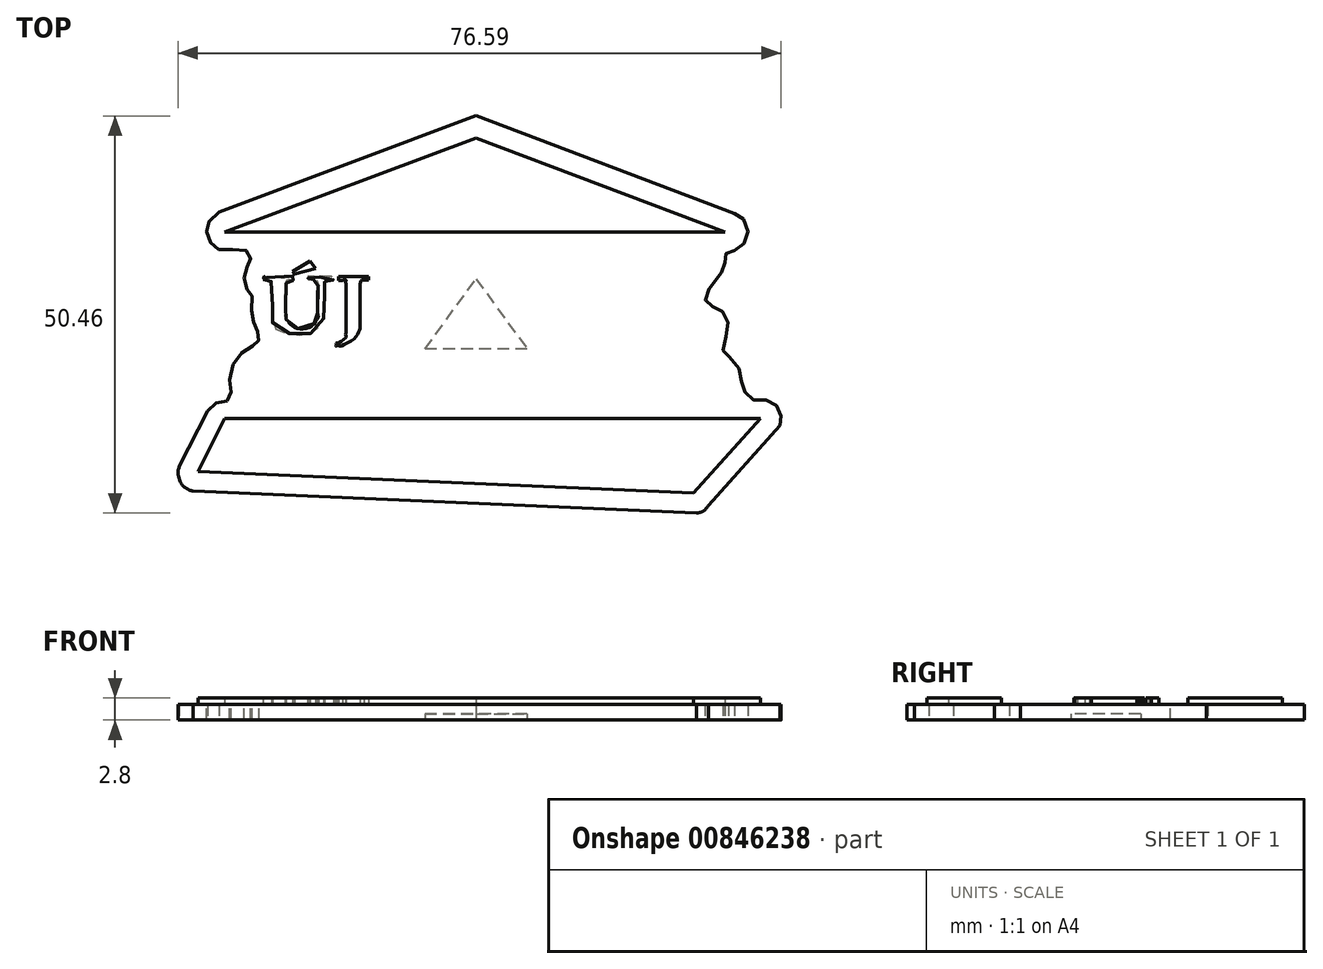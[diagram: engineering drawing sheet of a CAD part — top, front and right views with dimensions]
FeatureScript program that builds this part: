
annotation { "Feature Type Name" : "Feature", "Feature Type Description" : "" }
export const myFeature = defineFeature(function(context is Context, id is Id, definition is map)
    precondition{}
    {
        {
            var Q0;
            Q0=qCreatedBy(makeId("Top.planeOp"),FACE);
            var sketch = newSketch(context, id + "F0", { "sketchPlane" : qUnion([Q0])});
            skLineSegment(sketch, "E0", {"start": v(-30.08, 10.5) * mm, "end": v(1.83, 22.46) * mm});
            skLineSegment(sketch, "E1", {"start": v(1.83, 22.46) * mm, "end": v(33.46, 10.5) * mm});
            skLineSegment(sketch, "E2", {"start": v(33.46, 10.5) * mm, "end": v(-30.08, 10.5) * mm});
            skLineSegment(sketch, "E3", {"start": v(-30.08, -13.2) * mm, "end": v(37.96, -13.19) * mm});
            skLineSegment(sketch, "E4", {"start": v(37.96, -13.19) * mm, "end": v(29.5, -22.68) * mm});
            skLineSegment(sketch, "E5", {"start": v(29.5, -22.68) * mm, "end": v(-33.48, -19.9) * mm});
            skLineSegment(sketch, "E6", {"start": v(-33.48, -19.9) * mm, "end": v(-30.08, -13.2) * mm});
            skFitSpline(sketch, "E7", {"points": [v(-25.1, 4.44) * mm, v(-24.51, 4.46) * mm, v(-24.23, 4.28) * mm, v(-24.13, 3.89) * mm, v(-24.05, 0) * mm, v(-24.04, -0.4) * mm, v(-23.47, -1.49) * mm, v(-21.36, -2.34) * mm, v(-19.33, -2.17) * mm, v(-17.82, -0.87) * mm, v(-17.52, 0.4) * mm, v(-17.44, 3.46) * mm, v(-17.44, 3.92) * mm, v(-17.28, 4.2) * mm, v(-16.7, 4.4) * mm, v(-16.38, 4.41) * mm, v(-16.38, 4.8) * mm, v(-16.52, 4.86) * mm, v(-19.36, 4.89) * mm, v(-19.5, 4.87) * mm, v(-19.5, 4.8) * mm, v(-19.5, 4.47) * mm, v(-19.49, 4.38) * mm, v(-19.23, 4.43) * mm, v(-18.68, 4.41) * mm, v(-18.33, 4.24) * mm, v(-18.19, 3.78) * mm, v(-18.19, 3.5) * mm, v(-18.2, 0.13) * mm, v(-18.2, -0.14) * mm, v(-18.42, -0.62) * mm, v(-19.42, -1.46) * mm, v(-20.82, -1.61) * mm, v(-21.7, -1.14) * mm, v(-22.28, -0.2) * mm, v(-22.3, 0.46) * mm, v(-22.3, 0.68) * mm, v(-22.28, 3.9) * mm, v(-22.25, 4.08) * mm, v(-22.12, 4.32) * mm, v(-21.64, 4.43) * mm, v(-21.37, 4.43) * mm, v(-21.31, 4.6) * mm, v(-21.34, 4.74) * mm, v(-21.34, 4.89) * mm, v(-21.52, 4.89) * mm, v(-24.93, 4.84) * mm, v(-25.08, 4.86) * mm, v(-25.13, 4.71) * mm, v(-25.1, 4.44) * mm]});
            skLineSegment(sketch, "E8", {"start": v(-21.44, 5.5) * mm, "end": v(-21.2, 5.16) * mm});
            skLineSegment(sketch, "E9", {"start": v(-21.2, 5.16) * mm, "end": v(-18.55, 5.87) * mm});
            skLineSegment(sketch, "E10", {"start": v(-18.55, 5.87) * mm, "end": v(-19.2, 6.79) * mm});
            skLineSegment(sketch, "E11", {"start": v(-19.2, 6.79) * mm, "end": v(-21.44, 5.5) * mm});
            skLineSegment(sketch, "E12", {"start": v(-15.1, 4.36) * mm, "end": v(-15.63, 4.36) * mm});
            skLineSegment(sketch, "E13", {"start": v(-15.63, 4.36) * mm, "end": v(-15.63, 4.86) * mm});
            skLineSegment(sketch, "E14", {"start": v(-15.63, 4.86) * mm, "end": v(-11.81, 4.86) * mm});
            skLineSegment(sketch, "E15", {"start": v(-11.81, 4.86) * mm, "end": v(-11.81, 4.4) * mm});
            skLineSegment(sketch, "E16", {"start": v(-11.81, 4.4) * mm, "end": v(-12.34, 4.4) * mm});
            skLineSegment(sketch, "E17", {"start": v(-14.68, 4.01) * mm, "end": v(-14.68, -2.04) * mm});
            skLineSegment(sketch, "E18", {"start": v(-12.84, 4) * mm, "end": v(-12.84, -1.76) * mm});
            skFitSpline(sketch, "E19", {"points": [v(-15.1, 4.36) * mm, v(-14.78, 4.36) * mm, v(-14.68, 4.01) * mm], "startDerivative": vector(0.76, 0.17) * mm, "endDerivative": vector(0.08, -0.96) * mm});
            skFitSpline(sketch, "E20", {"points": [v(-12.84, 4) * mm, v(-12.68, 4.32) * mm, v(-12.34, 4.4) * mm], "startDerivative": vector(0.22, 0.75) * mm, "endDerivative": vector(0.8, 0.04) * mm});
            skFitSpline(sketch, "E21", {"points": [v(-14.68, -2.04) * mm, v(-14.68, -2.66) * mm, v(-14.68, -2.79) * mm, v(-15.17, -3.3) * mm, v(-15.78, -3.58) * mm, v(-15.9, -3.58) * mm, v(-15.89, -3.66) * mm, v(-15.9, -3.93) * mm, v(-15.78, -3.95) * mm, v(-15.43, -3.95) * mm, v(-14.92, -3.79) * mm, v(-13.75, -3.09) * mm, v(-13.2, -2.47) * mm, v(-12.84, -1.76) * mm], "startDerivative": vector(-0.26, -8.21) * mm, "endDerivative": vector(3.35, 7.13) * mm});
            skLineSegment(sketch, "E22", {"start": v(-8.39, 6.17) * mm, "end": v(-8.85, 6.17) * mm});
            skLineSegment(sketch, "E23", {"start": v(-8.85, 6.17) * mm, "end": v(-8.85, 6.78) * mm});
            skLineSegment(sketch, "E24", {"start": v(-8.85, 6.78) * mm, "end": v(-2.66, 6.78) * mm});
            skLineSegment(sketch, "E25", {"start": v(-2.66, 6.78) * mm, "end": v(-2.66, 6.17) * mm});
            skLineSegment(sketch, "E26", {"start": v(-2.66, 6.17) * mm, "end": v(-3.36, 6.17) * mm});
            skLineSegment(sketch, "E27", {"start": v(-7.13, 5.37) * mm, "end": v(-7.13, -2.82) * mm});
            skLineSegment(sketch, "E28", {"start": v(-4.27, 5.39) * mm, "end": v(-4.27, 2.06) * mm});
            skLineSegment(sketch, "E29", {"start": v(-4.27, 2.06) * mm, "end": v(0.72, 2.06) * mm});
            skLineSegment(sketch, "E30", {"start": v(0.72, 2.06) * mm, "end": v(0.72, 5.28) * mm});
            skLineSegment(sketch, "E31", {"start": v(-0.41, 6.13) * mm, "end": v(-0.88, 6.13) * mm});
            skLineSegment(sketch, "E32", {"start": v(-0.88, 6.13) * mm, "end": v(-0.88, 6.7) * mm});
            skLineSegment(sketch, "E33", {"start": v(-0.88, 6.7) * mm, "end": v(5.27, 6.7) * mm});
            skLineSegment(sketch, "E34", {"start": v(5.27, 6.7) * mm, "end": v(5.27, 6.19) * mm});
            skLineSegment(sketch, "E35", {"start": v(5.27, 6.19) * mm, "end": v(4.53, 6.19) * mm});
            skLineSegment(sketch, "E36", {"start": v(3.5, 5.2) * mm, "end": v(3.5, -2.7) * mm});
            skLineSegment(sketch, "E37", {"start": v(-4.28, -2.78) * mm, "end": v(-4.28, 1.1) * mm});
            skLineSegment(sketch, "E38", {"start": v(-4.28, 1.1) * mm, "end": v(0.7, 1.1) * mm});
            skLineSegment(sketch, "E39", {"start": v(0.7, 1.1) * mm, "end": v(0.7, -2.6) * mm});
            skLineSegment(sketch, "E40", {"start": v(-8.5, -3.66) * mm, "end": v(-8.85, -3.66) * mm});
            skLineSegment(sketch, "E41", {"start": v(-8.85, -3.66) * mm, "end": v(-8.85, -4.23) * mm});
            skLineSegment(sketch, "E42", {"start": v(-8.85, -4.23) * mm, "end": v(-2.68, -4.23) * mm});
            skLineSegment(sketch, "E43", {"start": v(-2.68, -4.23) * mm, "end": v(-2.68, -3.75) * mm});
            skLineSegment(sketch, "E44", {"start": v(-2.68, -3.75) * mm, "end": v(-3.08, -3.75) * mm});
            skLineSegment(sketch, "E45", {"start": v(-0.67, -3.75) * mm, "end": v(-1, -3.75) * mm});
            skLineSegment(sketch, "E46", {"start": v(-1, -3.75) * mm, "end": v(-1, -4.23) * mm});
            skLineSegment(sketch, "E47", {"start": v(-1, -4.23) * mm, "end": v(5.21, -4.23) * mm});
            skLineSegment(sketch, "E48", {"start": v(5.21, -4.23) * mm, "end": v(5.21, -3.75) * mm});
            skLineSegment(sketch, "E49", {"start": v(5.21, -3.75) * mm, "end": v(4.72, -3.75) * mm});
            skLineSegment(sketch, "E50", {"start": v(6.1, -3.75) * mm, "end": v(5.78, -3.75) * mm});
            skLineSegment(sketch, "E51", {"start": v(5.78, -3.75) * mm, "end": v(5.78, -4.23) * mm});
            skLineSegment(sketch, "E52", {"start": v(5.78, -4.23) * mm, "end": v(10.42, -4.23) * mm});
            skLineSegment(sketch, "E53", {"start": v(10.42, -4.23) * mm, "end": v(10.42, -3.75) * mm});
            skLineSegment(sketch, "E54", {"start": v(10.42, -3.75) * mm, "end": v(10.07, -3.75) * mm});
            skLineSegment(sketch, "E55", {"start": v(7.73, -2.6) * mm, "end": v(12.18, 6.83) * mm});
            skLineSegment(sketch, "E56", {"start": v(12.18, 6.83) * mm, "end": v(13.26, 6.83) * mm});
            skLineSegment(sketch, "E57", {"start": v(13.26, 6.83) * mm, "end": v(17.45, -2.7) * mm});
            skLineSegment(sketch, "E58", {"start": v(10.22, 0) * mm, "end": v(11.72, 3.76) * mm});
            skLineSegment(sketch, "E59", {"start": v(11.72, 3.76) * mm, "end": v(13.22, 0) * mm});
            skLineSegment(sketch, "E60", {"start": v(13.22, 0) * mm, "end": v(10.22, 0) * mm});
            skLineSegment(sketch, "E61", {"start": v(8.99, -3) * mm, "end": v(9.81, -0.88) * mm});
            skLineSegment(sketch, "E62", {"start": v(9.81, -0.88) * mm, "end": v(13.66, -0.88) * mm});
            skLineSegment(sketch, "E63", {"start": v(13.66, -0.88) * mm, "end": v(14.56, -3.07) * mm});
            skLineSegment(sketch, "E64", {"start": v(13.8, -3.75) * mm, "end": v(13.43, -3.75) * mm});
            skLineSegment(sketch, "E65", {"start": v(13.43, -3.75) * mm, "end": v(13.43, -4.23) * mm});
            skLineSegment(sketch, "E66", {"start": v(13.43, -4.23) * mm, "end": v(19.3, -4.23) * mm});
            skLineSegment(sketch, "E67", {"start": v(19.3, -4.23) * mm, "end": v(19.3, -3.75) * mm});
            skLineSegment(sketch, "E68", {"start": v(19.3, -3.75) * mm, "end": v(18.88, -3.75) * mm});
            skLineSegment(sketch, "E69", {"start": v(11.34, 7.83) * mm, "end": v(11.73, 7.26) * mm});
            skLineSegment(sketch, "E70", {"start": v(11.73, 7.26) * mm, "end": v(16.2, 8.38) * mm});
            skLineSegment(sketch, "E71", {"start": v(16.2, 8.38) * mm, "end": v(15.06, 9.86) * mm});
            skLineSegment(sketch, "E72", {"start": v(15.06, 9.86) * mm, "end": v(11.34, 7.83) * mm});
            skLineSegment(sketch, "E73", {"start": v(23.23, 6.07) * mm, "end": v(27.17, 6.07) * mm});
            skLineSegment(sketch, "E74", {"start": v(27.17, 6.07) * mm, "end": v(19.8, -3.96) * mm});
            skLineSegment(sketch, "E75", {"start": v(19.8, -3.96) * mm, "end": v(20, -4.32) * mm});
            skLineSegment(sketch, "E76", {"start": v(20, -4.32) * mm, "end": v(30.47, -4.32) * mm});
            skLineSegment(sketch, "E77", {"start": v(30.47, -4.32) * mm, "end": v(31.28, -1.27) * mm});
            skLineSegment(sketch, "E78", {"start": v(31.28, -1.27) * mm, "end": v(30.49, -1.27) * mm});
            skLineSegment(sketch, "E79", {"start": v(30.49, -1.27) * mm, "end": v(29.93, -2.28) * mm});
            skLineSegment(sketch, "E80", {"start": v(27.89, -3.5) * mm, "end": v(23.51, -3.5) * mm});
            skLineSegment(sketch, "E81", {"start": v(23.51, -3.5) * mm, "end": v(30.8, 6.4) * mm});
            skLineSegment(sketch, "E82", {"start": v(30.8, 6.4) * mm, "end": v(30.6, 6.77) * mm});
            skLineSegment(sketch, "E83", {"start": v(30.6, 6.77) * mm, "end": v(22.29, 6.77) * mm});
            skLineSegment(sketch, "E84", {"start": v(21.5, 7.2) * mm, "end": v(20.84, 7.2) * mm});
            skLineSegment(sketch, "E85", {"start": v(20.84, 7.2) * mm, "end": v(20.84, 3.95) * mm});
            skLineSegment(sketch, "E86", {"start": v(20.84, 3.95) * mm, "end": v(21.5, 3.95) * mm});
            skFitSpline(sketch, "E87", {"points": [v(-8.39, 6.17) * mm, v(-7.89, 6.17) * mm, v(-7.38, 5.86) * mm, v(-7.13, 5.37) * mm], "startDerivative": vector(1.55, 0.19) * mm, "endDerivative": vector(0.57, -1.56) * mm});
            skFitSpline(sketch, "E88", {"points": [v(-4.27, 5.39) * mm, v(-4.1, 5.83) * mm, v(-3.74, 6.05) * mm, v(-3.36, 6.17) * mm], "startDerivative": vector(0.33, 1.4) * mm, "endDerivative": vector(1.17, 0.33) * mm});
            skFitSpline(sketch, "E89", {"points": [v(-7.13, -2.82) * mm, v(-7.28, -3.3) * mm, v(-7.7, -3.6) * mm, v(-8.23, -3.66) * mm, v(-8.5, -3.66) * mm], "startDerivative": vector(-0.35, -1.9) * mm, "endDerivative": vector(-1.25, 0.02) * mm});
            skFitSpline(sketch, "E90", {"points": [v(-4.28, -2.78) * mm, v(-4.1, -3.18) * mm, v(-3.76, -3.5) * mm, v(-3.08, -3.75) * mm], "startDerivative": vector(0.48, -1.4) * mm, "endDerivative": vector(1.91, -0.58) * mm});
            skFitSpline(sketch, "E91", {"points": [v(-0.67, -3.75) * mm, v(-0.24, -3.75) * mm, v(0.3, -3.66) * mm, v(0.65, -3.2) * mm, v(0.7, -2.6) * mm], "startDerivative": vector(1.82, 0) * mm, "endDerivative": vector(-0.04, 2.27) * mm});
            skFitSpline(sketch, "E92", {"points": [v(3.5, -2.7) * mm, v(3.72, -3.17) * mm, v(4.05, -3.48) * mm, v(4.41, -3.66) * mm, v(4.72, -3.75) * mm], "startDerivative": vector(0.63, -1.81) * mm, "endDerivative": vector(1.39, -0.34) * mm});
            skFitSpline(sketch, "E93", {"points": [v(6.1, -3.75) * mm, v(6.63, -3.75) * mm, v(7.2, -3.43) * mm, v(7.73, -2.6) * mm], "startDerivative": vector(1.82, -0.19) * mm, "endDerivative": vector(1.2, 2.39) * mm});
            skFitSpline(sketch, "E94", {"points": [v(8.99, -3) * mm, v(8.99, -3.18) * mm, v(9.13, -3.44) * mm, v(9.5, -3.63) * mm, v(10.07, -3.75) * mm], "startDerivative": vector(-0.22, -1.52) * mm, "endDerivative": vector(2.37, -0.06) * mm});
            skFitSpline(sketch, "E95", {"points": [v(-0.41, 6.13) * mm, v(0, 6.13) * mm, v(0.32, 5.98) * mm, v(0.54, 5.77) * mm, v(0.67, 5.45) * mm, v(0.72, 5.28) * mm], "startDerivative": vector(1.85, 0.19) * mm, "endDerivative": vector(0.28, -1) * mm});
            skFitSpline(sketch, "E96", {"points": [v(3.5, 5.2) * mm, v(3.5, 5.55) * mm, v(3.71, 5.87) * mm, v(4.07, 6.13) * mm, v(4.53, 6.19) * mm], "startDerivative": vector(-0.19, 1.53) * mm, "endDerivative": vector(1.8, 0.02) * mm});
            skFitSpline(sketch, "E97", {"points": [v(13.8, -3.75) * mm, v(14.03, -3.75) * mm, v(14.36, -3.59) * mm, v(14.5, -3.41) * mm, v(14.56, -3.07) * mm], "startDerivative": vector(0.97, -0.13) * mm, "endDerivative": vector(0.08, 1.38) * mm});
            skFitSpline(sketch, "E98", {"points": [v(17.45, -2.7) * mm, v(17.64, -2.98) * mm, v(17.94, -3.34) * mm, v(18.22, -3.52) * mm, v(18.6, -3.68) * mm, v(18.88, -3.75) * mm], "startDerivative": vector(0.89, -1.38) * mm, "endDerivative": vector(1.49, -0.33) * mm});
            skFitSpline(sketch, "E99", {"points": [v(21.5, 7.2) * mm, v(21.67, 6.98) * mm, v(21.93, 6.8) * mm, v(22.29, 6.77) * mm], "startDerivative": vector(0.55, -0.66) * mm, "endDerivative": vector(1.06, 0.06) * mm});
            skFitSpline(sketch, "E100", {"points": [v(21.5, 3.95) * mm, v(21.57, 4.4) * mm, v(21.78, 4.93) * mm, v(22.1, 5.4) * mm, v(22.64, 5.85) * mm, v(23.23, 6.07) * mm], "startDerivative": vector(0.3, 2.51) * mm, "endDerivative": vector(2.87, 0.8) * mm});
            skFitSpline(sketch, "E101", {"points": [v(27.89, -3.5) * mm, v(28.28, -3.5) * mm, v(28.84, -3.34) * mm, v(29.28, -3.05) * mm, v(29.7, -2.6) * mm, v(29.93, -2.28) * mm], "startDerivative": vector(2.09, -0.14) * mm, "endDerivative": vector(1.15, 1.72) * mm});
            skFitSpline(sketch, "E102", {"points": [v(-18.55, -5.16) * mm, v(-19.5, -5.13) * mm, v(-21.12, -5.07) * mm, v(-22, -5.07) * mm, v(-22.58, -5.12) * mm, v(-23.16, -5.22) * mm, v(-23.92, -5.38) * mm, v(-24.9, -5.72) * mm, v(-25.9, -6.27) * mm, v(-26.51, -6.9) * mm, v(-26.87, -7.57) * mm, v(-27, -8.39) * mm, v(-26.85, -9.23) * mm, v(-26.55, -9.8) * mm, v(-26.01, -10.28) * mm, v(-25.25, -10.75) * mm, v(-23.93, -11.23) * mm, v(-22.44, -11.46) * mm, v(-20.86, -11.5) * mm, v(-19.93, -11.43) * mm, v(-19.02, -11.34) * mm, v(-18.6, -11.26) * mm, v(-18.57, -11.26) * mm, v(-18.48, -11.07) * mm, v(-18.1, -10.43) * mm, v(-17.75, -9.8) * mm, v(-17.71, -9.74) * mm, v(-17.8, -9.71) * mm, v(-18.35, -9.68) * mm, v(-18.4, -9.67) * mm, v(-18.46, -9.74) * mm, v(-18.56, -9.88) * mm, v(-18.93, -10.27) * mm, v(-19.68, -10.75) * mm, v(-20.35, -10.95) * mm, v(-21.57, -11) * mm, v(-22.99, -10.7) * mm, v(-23.78, -10.03) * mm, v(-24.3, -9.17) * mm, v(-24.47, -7.92) * mm, v(-24.2, -6.98) * mm, v(-23.84, -6.46) * mm, v(-23.06, -5.94) * mm, v(-22.3, -5.64) * mm, v(-21.27, -5.47) * mm, v(-20.47, -5.49) * mm, v(-20, -5.61) * mm, v(-19.36, -5.96) * mm, v(-18.97, -6.34) * mm, v(-18.7, -6.63) * mm, v(-18.63, -6.81) * mm, v(-18.62, -6.84) * mm, v(-18.53, -6.87) * mm, v(-18.08, -6.84) * mm, v(-18.05, -6.82) * mm, v(-18.08, -6.52) * mm, v(-18.1, -6.12) * mm, v(-18.13, -5.6) * mm, v(-18.22, -5.17) * mm, v(-18.55, -5.16) * mm]});
            skLineSegment(sketch, "E103", {"start": v(-14.56, -8.57) * mm, "end": v(-12.39, -8.57) * mm});
            skLineSegment(sketch, "E104", {"start": v(-14.61, -9) * mm, "end": v(-10.44, -9) * mm});
            skLineSegment(sketch, "E105", {"start": v(-9.34, -11) * mm, "end": v(-9.63, -11) * mm});
            skLineSegment(sketch, "E106", {"start": v(-9.63, -11) * mm, "end": v(-9.63, -11.37) * mm});
            skLineSegment(sketch, "E107", {"start": v(-9.63, -11.37) * mm, "end": v(-5.63, -11.37) * mm});
            skLineSegment(sketch, "E108", {"start": v(-5.63, -11.37) * mm, "end": v(-5.63, -10.98) * mm});
            skLineSegment(sketch, "E109", {"start": v(-5.63, -10.98) * mm, "end": v(-5.8, -11) * mm});
            skLineSegment(sketch, "E110", {"start": v(-8.57, -7.94) * mm, "end": v(-8.57, -10.62) * mm});
            skLineSegment(sketch, "E111", {"start": v(-6.5, -7.96) * mm, "end": v(-6.5, -10.59) * mm});
            skLineSegment(sketch, "E112", {"start": v(-4.21, -8.3) * mm, "end": v(-4.21, -10.74) * mm});
            skLineSegment(sketch, "E113", {"start": v(-4.69, -10.98) * mm, "end": v(-4.98, -10.98) * mm});
            skLineSegment(sketch, "E114", {"start": v(-4.98, -10.98) * mm, "end": v(-4.98, -11.37) * mm});
            skLineSegment(sketch, "E115", {"start": v(-4.98, -11.37) * mm, "end": v(-1.1, -11.37) * mm});
            skLineSegment(sketch, "E116", {"start": v(-1.1, -11.37) * mm, "end": v(-1.1, -10.98) * mm});
            skLineSegment(sketch, "E117", {"start": v(-1.1, -10.98) * mm, "end": v(-1.33, -10.98) * mm});
            skLineSegment(sketch, "E118", {"start": v(-2.04, -8.28) * mm, "end": v(-2.04, -10.69) * mm});
            skLineSegment(sketch, "E119", {"start": v(2.64, -10.35) * mm, "end": v(2.64, -7.53) * mm});
            skLineSegment(sketch, "E120", {"start": v(2.64, -7.53) * mm, "end": v(4.31, -7.53) * mm});
            skLineSegment(sketch, "E121", {"start": v(4.31, -7.53) * mm, "end": v(4.31, -7.02) * mm});
            skLineSegment(sketch, "E122", {"start": v(4.31, -7.02) * mm, "end": v(2.64, -7.02) * mm});
            skLineSegment(sketch, "E123", {"start": v(2.64, -7.02) * mm, "end": v(2.64, -5.7) * mm});
            skLineSegment(sketch, "E124", {"start": v(2.64, -5.7) * mm, "end": v(2.15, -5.7) * mm});
            skLineSegment(sketch, "E125", {"start": v(2.15, -5.7) * mm, "end": v(0.43, -6.4) * mm});
            skLineSegment(sketch, "E126", {"start": v(0.43, -6.4) * mm, "end": v(0.43, -7.02) * mm});
            skLineSegment(sketch, "E127", {"start": v(0.43, -7.02) * mm, "end": v(-0.2, -7.02) * mm});
            skLineSegment(sketch, "E128", {"start": v(-0.2, -7.02) * mm, "end": v(-0.73, -7.53) * mm});
            skLineSegment(sketch, "E129", {"start": v(-0.73, -7.53) * mm, "end": v(0.43, -7.53) * mm});
            skLineSegment(sketch, "E130", {"start": v(0.43, -7.53) * mm, "end": v(0.43, -10.53) * mm});
            skLineSegment(sketch, "E131", {"start": v(6.13, -8.07) * mm, "end": v(6.13, -10.53) * mm});
            skLineSegment(sketch, "E132", {"start": v(8.26, -8.42) * mm, "end": v(8.26, -10.6) * mm});
            skLineSegment(sketch, "E133", {"start": v(5.37, -11) * mm, "end": v(5.06, -11) * mm});
            skLineSegment(sketch, "E134", {"start": v(5.06, -11) * mm, "end": v(5.06, -11.36) * mm});
            skLineSegment(sketch, "E135", {"start": v(5.06, -11.36) * mm, "end": v(9.5, -11.36) * mm});
            skLineSegment(sketch, "E136", {"start": v(9.5, -11.36) * mm, "end": v(9.5, -10.98) * mm});
            skLineSegment(sketch, "E137", {"start": v(9.5, -10.98) * mm, "end": v(8.93, -10.98) * mm});
            skLineSegment(sketch, "E138", {"start": v(8.26, -7.93) * mm, "end": v(8.26, -6.9) * mm});
            skLineSegment(sketch, "E139", {"start": v(5.53, -7.62) * mm, "end": v(5.24, -7.62) * mm});
            skLineSegment(sketch, "E140", {"start": v(5.24, -7.62) * mm, "end": v(5.24, -7.3) * mm});
            skLineSegment(sketch, "E141", {"start": v(5.24, -7.3) * mm, "end": v(6.13, -7.3) * mm});
            skLineSegment(sketch, "E142", {"start": v(14.85, -9.91) * mm, "end": v(14.85, -7.04) * mm});
            skLineSegment(sketch, "E143", {"start": v(14.85, -7.04) * mm, "end": v(11.89, -7.14) * mm});
            skLineSegment(sketch, "E144", {"start": v(11.89, -7.14) * mm, "end": v(11.9, -7.54) * mm});
            skLineSegment(sketch, "E145", {"start": v(12.77, -7.86) * mm, "end": v(12.77, -10.35) * mm});
            skLineSegment(sketch, "E146", {"start": v(19.3, -10.56) * mm, "end": v(19.3, -7.08) * mm});
            skLineSegment(sketch, "E147", {"start": v(19.3, -7.08) * mm, "end": v(16.1, -7.17) * mm});
            skLineSegment(sketch, "E148", {"start": v(16.1, -7.17) * mm, "end": v(16.11, -7.5) * mm});
            skLineSegment(sketch, "E149", {"start": v(17.07, -7.77) * mm, "end": v(17.07, -10.43) * mm});
            skLineSegment(sketch, "E150", {"start": v(17.06, -10.88) * mm, "end": v(17.06, -11.45) * mm});
            skLineSegment(sketch, "E151", {"start": v(21.75, -7.23) * mm, "end": v(21.11, -7.23) * mm});
            skLineSegment(sketch, "E152", {"start": v(21.11, -7.23) * mm, "end": v(21.12, -7.6) * mm});
            skLineSegment(sketch, "E153", {"start": v(21.12, -7.6) * mm, "end": v(21.56, -7.6) * mm});
            skLineSegment(sketch, "E154", {"start": v(21.94, -7.89) * mm, "end": v(21.94, -10.72) * mm});
            skLineSegment(sketch, "E155", {"start": v(24.11, -8.08) * mm, "end": v(24.11, -10.75) * mm});
            skLineSegment(sketch, "E156", {"start": v(26.3, -8.31) * mm, "end": v(26.3, -10.76) * mm});
            skLineSegment(sketch, "E157", {"start": v(28.55, -8.04) * mm, "end": v(28.55, -10.73) * mm});
            skLineSegment(sketch, "E158", {"start": v(30.73, -8.35) * mm, "end": v(30.73, -10.82) * mm});
            skLineSegment(sketch, "E159", {"start": v(32.95, -8.3) * mm, "end": v(32.95, -10.75) * mm});
            skLineSegment(sketch, "E160", {"start": v(21.07, -11.02) * mm, "end": v(20.93, -11.02) * mm});
            skLineSegment(sketch, "E161", {"start": v(20.93, -11.02) * mm, "end": v(20.93, -11.4) * mm});
            skLineSegment(sketch, "E162", {"start": v(20.93, -11.4) * mm, "end": v(24.9, -11.4) * mm});
            skLineSegment(sketch, "E163", {"start": v(24.9, -11.4) * mm, "end": v(24.88, -11) * mm});
            skLineSegment(sketch, "E164", {"start": v(24.88, -11) * mm, "end": v(24.61, -11.02) * mm});
            skLineSegment(sketch, "E165", {"start": v(25.73, -11) * mm, "end": v(25.55, -11) * mm});
            skLineSegment(sketch, "E166", {"start": v(25.55, -11) * mm, "end": v(25.55, -11.4) * mm});
            skLineSegment(sketch, "E167", {"start": v(25.55, -11.4) * mm, "end": v(29.38, -11.4) * mm});
            skLineSegment(sketch, "E168", {"start": v(29.38, -11.4) * mm, "end": v(29.36, -11) * mm});
            skLineSegment(sketch, "E169", {"start": v(29.36, -11) * mm, "end": v(29.06, -11.02) * mm});
            skLineSegment(sketch, "E170", {"start": v(30.22, -11) * mm, "end": v(29.94, -11) * mm});
            skLineSegment(sketch, "E171", {"start": v(29.94, -11) * mm, "end": v(29.94, -11.4) * mm});
            skLineSegment(sketch, "E172", {"start": v(29.94, -11.4) * mm, "end": v(33.83, -11.4) * mm});
            skLineSegment(sketch, "E173", {"start": v(33.83, -11.4) * mm, "end": v(33.83, -10.97) * mm});
            skLineSegment(sketch, "E174", {"start": v(33.83, -10.97) * mm, "end": v(33.61, -10.98) * mm});
            skLineSegment(sketch, "E175", {"start": v(24.15, -7.62) * mm, "end": v(24.15, -6.96) * mm});
            skFitSpline(sketch, "E176", {"points": [v(33.61, -10.98) * mm, v(33.42, -10.98) * mm, v(33.1, -10.86) * mm, v(32.95, -10.75) * mm], "startDerivative": vector(-0.59, -0.06) * mm, "endDerivative": vector(-0.4, 0.42) * mm});
            skFitSpline(sketch, "E177", {"points": [v(32.95, -8.3) * mm, v(32.85, -7.9) * mm, v(32.66, -7.6) * mm, v(32.23, -7.27) * mm, v(31.7, -7.1) * mm, v(31.1, -6.98) * mm, v(30.3, -7) * mm, v(29.68, -7.15) * mm, v(29.1, -7.4) * mm, v(28.67, -7.62) * mm, v(28.4, -7.78) * mm, v(28.36, -7.79) * mm, v(28.32, -7.7) * mm, v(27.99, -7.33) * mm, v(27.45, -7.06) * mm, v(26.78, -6.96) * mm, v(25.91, -7) * mm, v(25.4, -7.11) * mm, v(24.68, -7.38) * mm, v(24.41, -7.52) * mm, v(24.15, -7.62) * mm], "startDerivative": vector(-1.81, 8.83) * mm, "endDerivative": vector(-7.1, -2.45) * mm});
            skFitSpline(sketch, "E178", {"points": [v(30.22, -11) * mm, v(30.4, -11) * mm, v(30.6, -10.96) * mm, v(30.73, -10.82) * mm], "startDerivative": vector(0.55, -0.04) * mm, "endDerivative": vector(0.32, 0.72) * mm});
            skFitSpline(sketch, "E179", {"points": [v(28.55, -10.73) * mm, v(28.68, -10.9) * mm, v(28.84, -10.97) * mm, v(29.06, -11.02) * mm], "startDerivative": vector(0.37, -0.56) * mm, "endDerivative": vector(0.68, -0.1) * mm});
            skFitSpline(sketch, "E180", {"points": [v(28.55, -8.04) * mm, v(28.7, -7.94) * mm, v(29.24, -7.76) * mm, v(29.59, -7.73) * mm, v(29.95, -7.73) * mm, v(30.43, -7.87) * mm, v(30.68, -8.15) * mm, v(30.73, -8.35) * mm], "startDerivative": vector(1.2, 0.86) * mm, "endDerivative": vector(1.1, -1.57) * mm});
            skFitSpline(sketch, "E181", {"points": [v(26.3, -8.31) * mm, v(26.23, -8.14) * mm, v(26.06, -7.96) * mm, v(25.87, -7.82) * mm, v(25.27, -7.7) * mm, v(24.9, -7.7) * mm, v(24.36, -7.86) * mm, v(24.19, -7.96) * mm, v(24.11, -8.08) * mm], "startDerivative": vector(-0.53, 1.8) * mm, "endDerivative": vector(-0.74, -1.45) * mm});
            skFitSpline(sketch, "E182", {"points": [v(25.73, -11) * mm, v(25.87, -11) * mm, v(26.05, -10.96) * mm, v(26.23, -10.86) * mm, v(26.3, -10.76) * mm], "startDerivative": vector(0.62, -0.04) * mm, "endDerivative": vector(0.28, 0.48) * mm});
            skFitSpline(sketch, "E183", {"points": [v(24.11, -10.75) * mm, v(24.17, -10.86) * mm, v(24.29, -10.96) * mm, v(24.5, -11) * mm, v(24.61, -11.02) * mm], "startDerivative": vector(0.2, -0.51) * mm, "endDerivative": vector(0.46, -0.05) * mm});
            skFitSpline(sketch, "E184", {"points": [v(24.15, -6.96) * mm, v(23.92, -7.04) * mm, v(22.83, -7.2) * mm, v(21.75, -7.23) * mm], "startDerivative": vector(-0.95, -0.4) * mm, "endDerivative": vector(-2.53, -0.03) * mm});
            skFitSpline(sketch, "E185", {"points": [v(21.56, -7.6) * mm, v(21.67, -7.65) * mm, v(21.86, -7.77) * mm, v(21.94, -7.89) * mm], "startDerivative": vector(0.36, -0.15) * mm, "endDerivative": vector(0.2, -0.4) * mm});
            skFitSpline(sketch, "E186", {"points": [v(21.94, -10.72) * mm, v(21.87, -10.8) * mm, v(21.68, -10.93) * mm, v(21.26, -11.02) * mm, v(21.07, -11.02) * mm], "startDerivative": vector(-0.28, -0.62) * mm, "endDerivative": vector(-0.73, 0.03) * mm});
            skFitSpline(sketch, "E187", {"points": [v(17.06, -11.45) * mm, v(17.7, -11.33) * mm, v(18.22, -11.26) * mm, v(18.78, -11.19) * mm, v(19.6, -11.1) * mm, v(20.24, -11.1) * mm, v(20.27, -11.09) * mm, v(20.27, -10.9) * mm, v(20.24, -10.72) * mm, v(19.91, -10.72) * mm, v(19.3, -10.56) * mm], "startDerivative": vector(3.34, 1) * mm, "endDerivative": vector(-2.67, 2.3) * mm});
            skFitSpline(sketch, "E188", {"points": [v(16.11, -7.5) * mm, v(16.3, -7.5) * mm, v(16.55, -7.5) * mm, v(16.84, -7.6) * mm, v(17.07, -7.77) * mm], "startDerivative": vector(0.84, -0.02) * mm, "endDerivative": vector(0.84, -0.69) * mm});
            skFitSpline(sketch, "E189", {"points": [v(14.85, -9.91) * mm, v(14.93, -10.17) * mm, v(15.05, -10.4) * mm, v(15.4, -10.67) * mm, v(15.7, -10.74) * mm, v(16.11, -10.75) * mm, v(16.52, -10.7) * mm, v(16.8, -10.6) * mm, v(17.07, -10.43) * mm], "startDerivative": vector(0.65, -2.37) * mm, "endDerivative": vector(2.2, 1.56) * mm});
            skFitSpline(sketch, "E190", {"points": [v(12.77, -10.35) * mm, v(12.77, -10.5) * mm, v(12.83, -10.66) * mm, v(12.98, -10.88) * mm, v(13.37, -11.15) * mm, v(13.88, -11.38) * mm, v(14.52, -11.47) * mm, v(15.32, -11.48) * mm, v(15.85, -11.36) * mm, v(16.43, -11.15) * mm, v(16.76, -11) * mm, v(17.06, -10.88) * mm], "startDerivative": vector(-0.25, -2.77) * mm, "endDerivative": vector(3.84, 1.33) * mm});
            skFitSpline(sketch, "E191", {"points": [v(11.9, -7.54) * mm, v(12.1, -7.54) * mm, v(12.4, -7.6) * mm, v(12.64, -7.7) * mm, v(12.77, -7.86) * mm], "startDerivative": vector(0.84, 0.04) * mm, "endDerivative": vector(0.44, -0.83) * mm});
            skFitSpline(sketch, "E192", {"points": [v(6.13, -7.3) * mm, v(6.3, -7.3) * mm, v(6.7, -7.23) * mm, v(7.26, -7.12) * mm, v(7.83, -6.98) * mm, v(8.26, -6.9) * mm], "startDerivative": vector(1.3, -0.06) * mm, "endDerivative": vector(2.6, 0.65) * mm});
            skFitSpline(sketch, "E193", {"points": [v(5.53, -7.62) * mm, v(5.66, -7.65) * mm, v(5.94, -7.73) * mm, v(6.07, -7.87) * mm, v(6.13, -8.07) * mm], "startDerivative": vector(0.58, -0.13) * mm, "endDerivative": vector(0.16, -0.83) * mm});
            skFitSpline(sketch, "E194", {"points": [v(6.13, -10.53) * mm, v(6.08, -10.68) * mm, v(5.97, -10.83) * mm, v(5.74, -10.96) * mm, v(5.49, -11.01) * mm, v(5.37, -11) * mm], "startDerivative": vector(-0.24, -0.84) * mm, "endDerivative": vector(-0.67, 0.05) * mm});
            skFitSpline(sketch, "E195", {"points": [v(8.26, -10.6) * mm, v(8.33, -10.78) * mm, v(8.47, -10.9) * mm, v(8.71, -10.96) * mm, v(8.93, -10.98) * mm], "startDerivative": vector(0.19, -0.8) * mm, "endDerivative": vector(0.81, -0.06) * mm});
            skFitSpline(sketch, "E196", {"points": [v(8.26, -7.93) * mm, v(8.42, -7.77) * mm, v(8.76, -7.45) * mm, v(9.12, -7.21) * mm, v(9.4, -7.05) * mm, v(9.84, -6.95) * mm, v(10.4, -6.96) * mm, v(10.76, -7.07) * mm, v(11.02, -7.25) * mm, v(11.15, -7.45) * mm, v(11.14, -7.64) * mm, v(11.04, -7.93) * mm, v(10.8, -8.17) * mm, v(10.54, -8.29) * mm, v(10.04, -8.35) * mm, v(9.8, -8.27) * mm, v(9.58, -8.12) * mm, v(9.37, -8.03) * mm, v(9.06, -8) * mm, v(8.86, -8.07) * mm, v(8.52, -8.27) * mm, v(8.26, -8.42) * mm], "startDerivative": vector(3.6, 3.57) * mm, "endDerivative": vector(-5.27, -3.1) * mm});
            skFitSpline(sketch, "E197", {"points": [v(0.43, -10.53) * mm, v(0.55, -10.8) * mm, v(0.84, -11.12) * mm, v(1.32, -11.34) * mm, v(2.07, -11.47) * mm, v(2.8, -11.46) * mm, v(3.75, -11.24) * mm, v(4.34, -11.07) * mm, v(4.5, -10.98) * mm, v(4.47, -10.79) * mm, v(4.35, -10.7) * mm, v(4.15, -10.69) * mm, v(3.9, -10.78) * mm, v(3.48, -10.86) * mm, v(3.02, -10.75) * mm, v(2.72, -10.6) * mm, v(2.64, -10.35) * mm], "startDerivative": vector(1.69, -5.06) * mm, "endDerivative": vector(-0.79, 5.58) * mm});
            skFitSpline(sketch, "E198", {"points": [v(-2.04, -10.69) * mm, v(-1.94, -10.84) * mm, v(-1.68, -10.98) * mm, v(-1.33, -10.98) * mm], "startDerivative": vector(0.27, -0.56) * mm, "endDerivative": vector(0.93, 0.1) * mm});
            skFitSpline(sketch, "E199", {"points": [v(-4.21, -10.74) * mm, v(-4.28, -10.87) * mm, v(-4.45, -10.97) * mm, v(-4.69, -10.98) * mm], "startDerivative": vector(-0.18, -0.49) * mm, "endDerivative": vector(-0.65, 0) * mm});
            skFitSpline(sketch, "E200", {"points": [v(-6.5, -7.96) * mm, v(-6.08, -7.84) * mm, v(-5.7, -7.68) * mm, v(-5.11, -7.63) * mm, v(-4.63, -7.74) * mm, v(-4.31, -8.06) * mm, v(-4.21, -8.3) * mm], "startDerivative": vector(2.11, 0.78) * mm, "endDerivative": vector(0.56, -1.73) * mm});
            skFitSpline(sketch, "E201", {"points": [v(-2.04, -8.28) * mm, v(-2.1, -7.91) * mm, v(-2.38, -7.54) * mm, v(-2.92, -7.2) * mm, v(-3.44, -7.03) * mm, v(-4.21, -6.93) * mm, v(-4.64, -6.97) * mm, v(-5.11, -7.07) * mm, v(-5.77, -7.31) * mm, v(-6.08, -7.44) * mm, v(-6.5, -7.64) * mm, v(-6.5, -7.58) * mm, v(-6.5, -7) * mm, v(-6.5, -7) * mm, v(-6.98, -7.03) * mm, v(-8.14, -7.24) * mm, v(-9.31, -7.27) * mm, v(-9.35, -7.27) * mm, v(-9.35, -7.35) * mm, v(-9.36, -7.63) * mm, v(-9.14, -7.61) * mm, v(-8.95, -7.61) * mm, v(-8.67, -7.7) * mm, v(-8.57, -7.94) * mm], "startDerivative": vector(-0.79, 8.64) * mm, "endDerivative": vector(1.7, -7.62) * mm});
            skFitSpline(sketch, "E202", {"points": [v(-6.5, -10.59) * mm, v(-6.34, -10.8) * mm, v(-6.11, -10.98) * mm, v(-5.8, -11) * mm], "startDerivative": vector(0.15, -0.59) * mm, "endDerivative": vector(0.88, 0.06) * mm});
            skFitSpline(sketch, "E203", {"points": [v(-8.57, -10.62) * mm, v(-8.64, -10.84) * mm, v(-8.96, -10.98) * mm, v(-9.34, -11) * mm], "startDerivative": vector(-0.1, -0.84) * mm, "endDerivative": vector(-1.04, 0.02) * mm});
            skFitSpline(sketch, "E204", {"points": [v(-10.44, -9) * mm, v(-10.34, -8.73) * mm, v(-10.36, -8.3) * mm, v(-11.18, -7.32) * mm, v(-12.23, -7.02) * mm, v(-13.54, -6.96) * mm, v(-14.74, -7.23) * mm, v(-15.54, -7.64) * mm, v(-16.34, -8.3) * mm, v(-16.68, -9.2) * mm, v(-16.56, -10.07) * mm, v(-16.02, -10.74) * mm, v(-14.94, -11.26) * mm, v(-13.9, -11.44) * mm, v(-12.63, -11.42) * mm, v(-11.92, -11.25) * mm, v(-11.02, -10.86) * mm, v(-10.57, -10.59) * mm, v(-10.44, -10.43) * mm, v(-10.44, -10.34) * mm, v(-10.67, -10.23) * mm, v(-10.82, -10.22) * mm, v(-11.02, -10.33) * mm, v(-11.3, -10.46) * mm, v(-11.73, -10.59) * mm], "startDerivative": vector(3.96, 9.4) * mm, "endDerivative": vector(-8.98, -1.29) * mm});
            skFitSpline(sketch, "E205", {"points": [v(-11.73, -10.59) * mm, v(-12.1, -10.63) * mm, v(-12.74, -10.65) * mm, v(-13.42, -10.52) * mm, v(-14.08, -10.22) * mm, v(-14.48, -9.7) * mm, v(-14.65, -9.34) * mm, v(-14.7, -9.14) * mm, v(-14.7, -9.01) * mm, v(-14.7, -8.98) * mm, v(-14.61, -9) * mm], "startDerivative": vector(-3.24, -0.47) * mm, "endDerivative": vector(2.24, -0.57) * mm});
            skFitSpline(sketch, "E206", {"points": [v(-14.56, -8.57) * mm, v(-14.56, -8.43) * mm, v(-14.51, -8.16) * mm, v(-14.29, -7.8) * mm, v(-13.96, -7.54) * mm, v(-13.6, -7.4) * mm, v(-12.96, -7.38) * mm, v(-12.75, -7.48) * mm, v(-12.62, -7.6) * mm, v(-12.46, -7.84) * mm, v(-12.34, -8.18) * mm, v(-12.33, -8.4) * mm, v(-12.33, -8.57) * mm, v(-12.39, -8.57) * mm], "startDerivative": vector(-0.08, 2.36) * mm, "endDerivative": vector(-2, 0.56) * mm});
            skLineSegment(sketch, "E207", {"start": v(-30.8, 13.04) * mm, "end": v(1.83, 25.26) * mm});
            skLineSegment(sketch, "E208", {"start": v(1.83, 25.26) * mm, "end": v(34.68, 12.85) * mm});
            skLineSegment(sketch, "E209", {"start": v(-32.25, -12.2) * mm, "end": v(-35.84, -19.3) * mm});
            skLineSegment(sketch, "E210", {"start": v(-34.12, -22.39) * mm, "end": v(29.85, -25.2) * mm});
            skLineSegment(sketch, "E211", {"start": v(31.4, -24.25) * mm, "end": v(40.45, -14.1) * mm});
            skFitSpline(sketch, "E212", {"points": [v(29.85, -25.2) * mm, v(30.3, -25.13) * mm, v(30.78, -24.92) * mm, v(31.4, -24.25) * mm], "startDerivative": vector(1.58, 0.17) * mm, "endDerivative": vector(1.52, 1.9) * mm});
            skFitSpline(sketch, "E213", {"points": [v(40.45, -14.1) * mm, v(40.57, -13.28) * mm, v(40.6, -12.96) * mm, v(40.45, -12.24) * mm, v(39.95, -11.47) * mm, v(38.99, -10.88) * mm, v(38.28, -10.82) * mm, v(37.1, -10.82) * mm, v(36.67, -10.73) * mm, v(35.85, -9.6) * mm, v(35.62, -9.21) * mm, v(35.54, -7.89) * mm, v(35.36, -7.02) * mm, v(34.4, -5.7) * mm, v(33.73, -5.15) * mm, v(33.32, -4.8) * mm, v(33.23, -4.19) * mm, v(33.63, -2.68) * mm, v(33.91, -1.34) * mm, v(33.65, -0.25) * mm, v(33.12, 0.43) * mm, v(32.45, 0.93) * mm, v(31.57, 1.1) * mm, v(31.11, 1.47) * mm, v(30.92, 2.12) * mm, v(31.04, 2.68) * mm, v(32.88, 5.13) * mm, v(33.14, 5.58) * mm, v(33.43, 6.35) * mm, v(33.43, 7.23) * mm, v(33.5, 7.61) * mm, v(33.8, 7.97) * mm, v(34.38, 8.15) * mm, v(34.95, 8.24) * mm, v(35.75, 8.86) * mm, v(36.28, 9.77) * mm, v(36.4, 10.93) * mm, v(35.92, 12.04) * mm, v(35.3, 12.55) * mm, v(34.68, 12.85) * mm], "startDerivative": vector(5.13, 37.38) * mm, "endDerivative": vector(-27.65, 11.7) * mm});
            skFitSpline(sketch, "E214", {"points": [v(-35.84, -19.3) * mm, v(-36, -19.97) * mm, v(-35.72, -21.2) * mm, v(-35.27, -21.84) * mm, v(-34.52, -22.29) * mm, v(-34.12, -22.39) * mm], "startDerivative": vector(-1.26, -3.15) * mm, "endDerivative": vector(2.5, -0.41) * mm});
            skFitSpline(sketch, "E215", {"points": [v(-32.25, -12.2) * mm, v(-31.62, -11.44) * mm, v(-30.95, -11.13) * mm, v(-30, -11.04) * mm, v(-29.54, -10.81) * mm, v(-29.23, -10.06) * mm, v(-29.4, -9.32) * mm, v(-29.42, -8.14) * mm, v(-29.13, -6.62) * mm, v(-28.25, -5.25) * mm, v(-27.57, -4.61) * mm, v(-26.53, -4) * mm, v(-26.07, -3.74) * mm, v(-25.8, -3.39) * mm, v(-25.74, -2.9) * mm, v(-25.77, -2.34) * mm, v(-26.04, -1.83) * mm, v(-26.28, -1.3) * mm, v(-26.57, -0.34) * mm, v(-26.63, 0.38) * mm, v(-26.6, 2.22) * mm, v(-26.6, 2.41) * mm, v(-26.7, 2.63) * mm, v(-27.12, 3.14) * mm, v(-27.43, 3.52) * mm, v(-27.62, 4.7) * mm, v(-27.52, 5.48) * mm, v(-27.08, 6.34) * mm, v(-26.87, 6.67) * mm, v(-26.77, 7.27) * mm, v(-27, 7.9) * mm, v(-27.47, 8.21) * mm, v(-28.14, 8.25) * mm, v(-30.57, 8.28) * mm, v(-30.78, 8.28) * mm, v(-31.29, 8.53) * mm, v(-31.87, 9.12) * mm, v(-32.25, 9.97) * mm, v(-32.35, 10.82) * mm, v(-32.25, 11.41) * mm, v(-31.84, 12.16) * mm, v(-30.8, 13.04) * mm], "startDerivative": vector(22.27, 31.02) * mm, "endDerivative": vector(44.3, 25.13) * mm});
            skSolve(sketch);
        }
        {
            var Q0;
            Q0=makeQuery(id+"F0.imprint","IMPRINT",FACE,{"disambiguationData":[TD([[makeQuery(id+"F0.imprint","IMPRINT",EDGE,{"derivedFrom":sQuery(id+"F0.wireOp",EDGE,"E0")}),1.0]])]});
            var Q1;
            Q1=makeQuery(id+"F0.imprint","IMPRINT",FACE,{"disambiguationData":[TD([[makeQuery(id+"F0.imprint","IMPRINT",EDGE,{"derivedFrom":sQuery(id+"F0.wireOp",EDGE,"E103")}),1.0]])]});
            var Q2;
            Q2=makeQuery(id+"F0.imprint","IMPRINT",FACE,{"disambiguationData":[TD([[makeQuery(id+"F0.imprint","IMPRINT",EDGE,{"derivedFrom":sQuery(id+"F0.wireOp",EDGE,"E58")}),-1.0]])]});
            var Q3;
            Q3=makeQuery(id+"F0.imprint","IMPRINT",FACE,{"disambiguationData":[TD([[makeQuery(id+"F0.imprint","IMPRINT",EDGE,{"derivedFrom":sQuery(id+"F0.wireOp",EDGE,"E0")}),-1.0]])]});
            var Q4;
            Q4=makeQuery(id+"F0.imprint","IMPRINT",FACE,{"disambiguationData":[TD([[makeQuery(id+"F0.imprint","IMPRINT",EDGE,{"derivedFrom":sQuery(id+"F0.wireOp",EDGE,"E3")}),-1.0]])]});
            var Q5;
            Q5=makeQuery(id+"F0.imprint","IMPRINT",FACE,{"disambiguationData":[TD([[makeQuery(id+"F0.imprint","IMPRINT",EDGE,{"derivedFrom":sQuery(id+"F0.wireOp",EDGE,"E7")}),1.0]])]});
            var Q6;
            Q6=makeQuery(id+"F0.imprint","IMPRINT",FACE,{"disambiguationData":[TD([[makeQuery(id+"F0.imprint","IMPRINT",EDGE,{"derivedFrom":sQuery(id+"F0.wireOp",EDGE,"E8")}),1.0]])]});
            var Q7;
            Q7=makeQuery(id+"F0.imprint","IMPRINT",FACE,{"disambiguationData":[TD([[makeQuery(id+"F0.imprint","IMPRINT",EDGE,{"derivedFrom":sQuery(id+"F0.wireOp",EDGE,"E12")}),-1.0]])]});
            var Q8;
            Q8=makeQuery(id+"F0.imprint","IMPRINT",FACE,{"disambiguationData":[TD([[makeQuery(id+"F0.imprint","IMPRINT",EDGE,{"derivedFrom":sQuery(id+"F0.wireOp",EDGE,"E22")}),-1.0]])]});
            var Q9;
            Q9=makeQuery(id+"F0.imprint","IMPRINT",FACE,{"disambiguationData":[TD([[makeQuery(id+"F0.imprint","IMPRINT",EDGE,{"derivedFrom":sQuery(id+"F0.wireOp",EDGE,"E50")}),1.0]])]});
            var Q10;
            Q10=makeQuery(id+"F0.imprint","IMPRINT",FACE,{"disambiguationData":[TD([[makeQuery(id+"F0.imprint","IMPRINT",EDGE,{"derivedFrom":sQuery(id+"F0.wireOp",EDGE,"E69")}),1.0]])]});
            var Q11;
            Q11=makeQuery(id+"F0.imprint","IMPRINT",FACE,{"disambiguationData":[TD([[makeQuery(id+"F0.imprint","IMPRINT",EDGE,{"derivedFrom":sQuery(id+"F0.wireOp",EDGE,"E105")}),1.0]])]});
            var Q12;
            Q12=makeQuery(id+"F0.imprint","IMPRINT",FACE,{"disambiguationData":[TD([[makeQuery(id+"F0.imprint","IMPRINT",EDGE,{"derivedFrom":sQuery(id+"F0.wireOp",EDGE,"E119")}),1.0]])]});
            var Q13;
            Q13=makeQuery(id+"F0.imprint","IMPRINT",FACE,{"disambiguationData":[TD([[makeQuery(id+"F0.imprint","IMPRINT",EDGE,{"derivedFrom":sQuery(id+"F0.wireOp",EDGE,"E131")}),1.0]])]});
            var Q14;
            Q14=makeQuery(id+"F0.imprint","IMPRINT",FACE,{"disambiguationData":[TD([[makeQuery(id+"F0.imprint","IMPRINT",EDGE,{"derivedFrom":sQuery(id+"F0.wireOp",EDGE,"E142")}),1.0]])]});
            var Q15;
            Q15=makeQuery(id+"F0.imprint","IMPRINT",FACE,{"disambiguationData":[TD([[makeQuery(id+"F0.imprint","IMPRINT",EDGE,{"derivedFrom":sQuery(id+"F0.wireOp",EDGE,"E151")}),1.0]])]});
            var Q16;
            Q16=makeQuery(id+"F0.imprint","IMPRINT",FACE,{"disambiguationData":[TD([[makeQuery(id+"F0.imprint","IMPRINT",EDGE,{"derivedFrom":sQuery(id+"F0.wireOp",EDGE,"E103")}),-1.0]])]});
            var Q17;
            Q17=makeQuery(id+"F0.imprint","IMPRINT",FACE,{"disambiguationData":[TD([[makeQuery(id+"F0.imprint","IMPRINT",EDGE,{"derivedFrom":sQuery(id+"F0.wireOp",EDGE,"E102")}),1.0]])]});
            var Q18;
            Q18=makeQuery(id+"F0.imprint","IMPRINT",FACE,{"disambiguationData":[TD([[makeQuery(id+"F0.imprint","IMPRINT",EDGE,{"derivedFrom":sQuery(id+"F0.wireOp",EDGE,"E73")}),1.0]])]});
            extrude(context, id + "F1", {"entities" : qUnion([Q0, Q1, Q2, Q3, Q4, Q5, Q6, Q7, Q8, Q9, Q10, Q11, Q12, Q13, Q14, Q15, Q16, Q17, Q18]), "depth" : 2 * mm, "offsetDistance" : 25 * mm});
        }
        {
            var Q0;
            Q0=makeQuery(id+"F1.opExtrude","CAP_FACE",FACE,{"disambiguationData":[OSD([sQuery(id+"F0.wireOp",EDGE,"E207"),sQuery(id+"F0.wireOp",EDGE,"E208"),sQuery(id+"F0.wireOp",EDGE,"E209"),sQuery(id+"F0.wireOp",EDGE,"E210"),sQuery(id+"F0.wireOp",EDGE,"E211"),sQuery(id+"F0.wireOp",EDGE,"E212"),sQuery(id+"F0.wireOp",EDGE,"E213"),sQuery(id+"F0.wireOp",EDGE,"E214"),sQuery(id+"F0.wireOp",EDGE,"E215")])],"isStart":false});
            var sketch = newSketch(context, id + "F2", { "sketchPlane" : qUnion([Q0])});
            skLineSegment(sketch, "E216.0.0", {"start": v(-30.08, 10.5) * mm, "end": v(33.46, 10.5) * mm});
            skLineSegment(sketch, "E216.0.1", {"start": v(33.46, 10.5) * mm, "end": v(1.83, 22.46) * mm});
            skLineSegment(sketch, "E216.0.2", {"start": v(1.83, 22.46) * mm, "end": v(-30.08, 10.5) * mm});
            skLineSegment(sketch, "E217.0.0", {"start": v(-30.08, -13.2) * mm, "end": v(-33.48, -19.9) * mm});
            skLineSegment(sketch, "E217.0.1", {"start": v(-33.48, -19.9) * mm, "end": v(29.5, -22.68) * mm});
            skLineSegment(sketch, "E217.0.2", {"start": v(29.5, -22.68) * mm, "end": v(37.96, -13.19) * mm});
            skLineSegment(sketch, "E217.0.3", {"start": v(37.96, -13.19) * mm, "end": v(-30.08, -13.2) * mm});
            skLineSegment(sketch, "E218.0.0", {"start": v(21.5, 7.2) * mm, "end": v(20.84, 7.2) * mm});
            skLineSegment(sketch, "E218.0.1", {"start": v(20.84, 7.2) * mm, "end": v(20.84, 3.95) * mm});
            skLineSegment(sketch, "E218.0.2", {"start": v(20.84, 3.95) * mm, "end": v(21.5, 3.95) * mm});
            skFitSpline(sketch, "E218.0.3", {"points": [v(21.5, 3.95) * mm, v(21.51, 4.1) * mm, v(21.55, 4.41) * mm, v(21.77, 4.95) * mm, v(22.09, 5.42) * mm, v(22.62, 5.9) * mm, v(23.03, 6.01) * mm, v(23.23, 6.07) * mm]});
            skLineSegment(sketch, "E218.0.4", {"start": v(23.23, 6.07) * mm, "end": v(27.17, 6.07) * mm});
            skLineSegment(sketch, "E218.0.5", {"start": v(27.17, 6.07) * mm, "end": v(19.8, -3.96) * mm});
            skLineSegment(sketch, "E218.0.6", {"start": v(19.8, -3.96) * mm, "end": v(20, -4.32) * mm});
            skLineSegment(sketch, "E218.0.7", {"start": v(20, -4.32) * mm, "end": v(30.47, -4.32) * mm});
            skLineSegment(sketch, "E218.0.8", {"start": v(30.47, -4.32) * mm, "end": v(31.28, -1.27) * mm});
            skLineSegment(sketch, "E218.0.9", {"start": v(31.28, -1.27) * mm, "end": v(30.49, -1.27) * mm});
            skLineSegment(sketch, "E218.0.10", {"start": v(30.49, -1.27) * mm, "end": v(29.93, -2.28) * mm});
            skFitSpline(sketch, "E218.0.11", {"points": [v(29.93, -2.28) * mm, v(29.87, -2.38) * mm, v(29.71, -2.6) * mm, v(29.29, -3.07) * mm, v(28.87, -3.36) * mm, v(28.28, -3.52) * mm, v(28, -3.5) * mm, v(27.89, -3.5) * mm]});
            skLineSegment(sketch, "E218.0.12", {"start": v(27.89, -3.5) * mm, "end": v(23.51, -3.5) * mm});
            skLineSegment(sketch, "E218.0.13", {"start": v(23.51, -3.5) * mm, "end": v(30.8, 6.4) * mm});
            skLineSegment(sketch, "E218.0.14", {"start": v(30.8, 6.4) * mm, "end": v(30.6, 6.77) * mm});
            skLineSegment(sketch, "E218.0.15", {"start": v(30.6, 6.77) * mm, "end": v(22.29, 6.77) * mm});
            skFitSpline(sketch, "E218.0.16", {"points": [v(22.29, 6.77) * mm, v(22.16, 6.76) * mm, v(21.92, 6.75) * mm, v(21.67, 6.98) * mm, v(21.55, 7.12) * mm, v(21.5, 7.2) * mm]});
            skLineSegment(sketch, "E219.0.0", {"start": v(19.3, -4.23) * mm, "end": v(19.3, -3.75) * mm});
            skLineSegment(sketch, "E219.0.1", {"start": v(19.3, -3.75) * mm, "end": v(18.88, -3.75) * mm});
            skFitSpline(sketch, "E219.0.2", {"points": [v(18.88, -3.75) * mm, v(18.8, -3.73) * mm, v(18.6, -3.7) * mm, v(18.21, -3.52) * mm, v(17.93, -3.36) * mm, v(17.63, -2.99) * mm, v(17.5, -2.8) * mm, v(17.45, -2.7) * mm]});
            skLineSegment(sketch, "E219.0.3", {"start": v(17.45, -2.7) * mm, "end": v(13.26, 6.83) * mm});
            skLineSegment(sketch, "E219.0.4", {"start": v(13.26, 6.83) * mm, "end": v(12.18, 6.83) * mm});
            skLineSegment(sketch, "E219.0.5", {"start": v(12.18, 6.83) * mm, "end": v(7.73, -2.6) * mm});
            skFitSpline(sketch, "E219.0.6", {"points": [v(7.73, -2.6) * mm, v(7.57, -2.9) * mm, v(7.28, -3.48) * mm, v(6.65, -3.8) * mm, v(6.28, -3.77) * mm, v(6.1, -3.75) * mm]});
            skLineSegment(sketch, "E219.0.7", {"start": v(6.1, -3.75) * mm, "end": v(5.78, -3.75) * mm});
            skLineSegment(sketch, "E219.0.8", {"start": v(5.78, -3.75) * mm, "end": v(5.78, -4.23) * mm});
            skLineSegment(sketch, "E219.0.9", {"start": v(5.78, -4.23) * mm, "end": v(10.42, -4.23) * mm});
            skLineSegment(sketch, "E219.0.10", {"start": v(10.42, -4.23) * mm, "end": v(10.42, -3.75) * mm});
            skLineSegment(sketch, "E219.0.11", {"start": v(10.42, -3.75) * mm, "end": v(10.07, -3.75) * mm});
            skFitSpline(sketch, "E219.0.12", {"points": [v(10.07, -3.75) * mm, v(9.82, -3.75) * mm, v(9.53, -3.64) * mm, v(9.11, -3.5) * mm, v(8.97, -3.17) * mm, v(8.97, -3.08) * mm, v(8.99, -3) * mm]});
            skLineSegment(sketch, "E219.0.13", {"start": v(8.99, -3) * mm, "end": v(9.81, -0.88) * mm});
            skLineSegment(sketch, "E219.0.14", {"start": v(9.81, -0.88) * mm, "end": v(13.66, -0.88) * mm});
            skLineSegment(sketch, "E219.0.15", {"start": v(13.66, -0.88) * mm, "end": v(14.56, -3.07) * mm});
            skFitSpline(sketch, "E219.0.16", {"points": [v(14.56, -3.07) * mm, v(14.55, -3.2) * mm, v(14.54, -3.42) * mm, v(14.38, -3.6) * mm, v(14.03, -3.79) * mm, v(13.87, -3.76) * mm, v(13.8, -3.75) * mm]});
            skLineSegment(sketch, "E219.0.17", {"start": v(13.8, -3.75) * mm, "end": v(13.43, -3.75) * mm});
            skLineSegment(sketch, "E219.0.18", {"start": v(13.43, -3.75) * mm, "end": v(13.43, -4.23) * mm});
            skLineSegment(sketch, "E219.0.19", {"start": v(13.43, -4.23) * mm, "end": v(19.3, -4.23) * mm});
            skFitSpline(sketch, "E220.0.2", {"points": [v(18.88, -3.75) * mm, v(18.8, -3.73) * mm, v(18.6, -3.7) * mm, v(18.21, -3.52) * mm, v(17.93, -3.36) * mm, v(17.63, -2.99) * mm, v(17.5, -2.8) * mm, v(17.45, -2.7) * mm]});
            skFitSpline(sketch, "E220.0.6", {"points": [v(7.73, -2.6) * mm, v(7.57, -2.9) * mm, v(7.28, -3.48) * mm, v(6.65, -3.8) * mm, v(6.28, -3.77) * mm, v(6.1, -3.75) * mm]});
            skFitSpline(sketch, "E220.0.12", {"points": [v(10.07, -3.75) * mm, v(9.82, -3.75) * mm, v(9.53, -3.64) * mm, v(9.11, -3.5) * mm, v(8.97, -3.17) * mm, v(8.97, -3.08) * mm, v(8.99, -3) * mm]});
            skFitSpline(sketch, "E220.0.16", {"points": [v(14.56, -3.07) * mm, v(14.55, -3.2) * mm, v(14.54, -3.42) * mm, v(14.38, -3.6) * mm, v(14.03, -3.79) * mm, v(13.87, -3.76) * mm, v(13.8, -3.75) * mm]});
            skLineSegment(sketch, "E221.0.0", {"start": v(10.22, 0) * mm, "end": v(13.22, 0) * mm});
            skLineSegment(sketch, "E221.0.1", {"start": v(13.22, 0) * mm, "end": v(11.72, 3.76) * mm});
            skLineSegment(sketch, "E221.0.2", {"start": v(11.72, 3.76) * mm, "end": v(10.22, 0) * mm});
            skLineSegment(sketch, "E222.0.0", {"start": v(5.21, -4.23) * mm, "end": v(5.21, -3.75) * mm});
            skLineSegment(sketch, "E222.0.1", {"start": v(5.21, -3.75) * mm, "end": v(4.72, -3.75) * mm});
            skFitSpline(sketch, "E222.0.2", {"points": [v(4.72, -3.75) * mm, v(4.62, -3.73) * mm, v(4.4, -3.68) * mm, v(4.04, -3.49) * mm, v(3.68, -3.2) * mm, v(3.57, -2.87) * mm, v(3.5, -2.7) * mm]});
            skLineSegment(sketch, "E222.0.3", {"start": v(3.5, -2.7) * mm, "end": v(3.5, 5.2) * mm});
            skFitSpline(sketch, "E222.0.4", {"points": [v(3.5, 5.2) * mm, v(3.5, 5.32) * mm, v(3.47, 5.56) * mm, v(3.7, 5.88) * mm, v(4.05, 6.18) * mm, v(4.37, 6.19) * mm, v(4.53, 6.19) * mm]});
            skLineSegment(sketch, "E222.0.5", {"start": v(4.53, 6.19) * mm, "end": v(5.27, 6.19) * mm});
            skLineSegment(sketch, "E222.0.6", {"start": v(5.27, 6.19) * mm, "end": v(5.27, 6.7) * mm});
            skLineSegment(sketch, "E222.0.7", {"start": v(5.27, 6.7) * mm, "end": v(-0.88, 6.7) * mm});
            skLineSegment(sketch, "E222.0.8", {"start": v(-0.88, 6.7) * mm, "end": v(-0.88, 6.13) * mm});
            skLineSegment(sketch, "E222.0.9", {"start": v(-0.88, 6.13) * mm, "end": v(-0.41, 6.13) * mm});
            skFitSpline(sketch, "E222.0.10", {"points": [v(-0.41, 6.13) * mm, v(-0.27, 6.14) * mm, v(0, 6.17) * mm, v(0.32, 5.98) * mm, v(0.56, 5.8) * mm, v(0.67, 5.45) * mm, v(0.7, 5.33) * mm, v(0.72, 5.28) * mm]});
            skLineSegment(sketch, "E222.0.11", {"start": v(0.72, 5.28) * mm, "end": v(0.72, 2.06) * mm});
            skLineSegment(sketch, "E222.0.12", {"start": v(0.72, 2.06) * mm, "end": v(-4.27, 2.06) * mm});
            skLineSegment(sketch, "E222.0.13", {"start": v(-4.27, 2.06) * mm, "end": v(-4.27, 5.39) * mm});
            skFitSpline(sketch, "E222.0.14", {"points": [v(-4.27, 5.39) * mm, v(-4.23, 5.55) * mm, v(-4.16, 5.87) * mm, v(-3.74, 6.06) * mm, v(-3.49, 6.13) * mm, v(-3.36, 6.17) * mm]});
            skLineSegment(sketch, "E222.0.15", {"start": v(-3.36, 6.17) * mm, "end": v(-2.66, 6.17) * mm});
            skLineSegment(sketch, "E222.0.16", {"start": v(-2.66, 6.17) * mm, "end": v(-2.66, 6.78) * mm});
            skLineSegment(sketch, "E222.0.17", {"start": v(-2.66, 6.78) * mm, "end": v(-8.85, 6.78) * mm});
            skLineSegment(sketch, "E222.0.18", {"start": v(-8.85, 6.78) * mm, "end": v(-8.85, 6.17) * mm});
            skLineSegment(sketch, "E222.0.19", {"start": v(-8.85, 6.17) * mm, "end": v(-8.39, 6.17) * mm});
            skFitSpline(sketch, "E222.0.20", {"points": [v(-8.39, 6.17) * mm, v(-8.22, 6.19) * mm, v(-7.88, 6.23) * mm, v(-7.32, 5.9) * mm, v(-7.2, 5.54) * mm, v(-7.13, 5.37) * mm]});
            skLineSegment(sketch, "E222.0.21", {"start": v(-7.13, 5.37) * mm, "end": v(-7.13, -2.82) * mm});
            skFitSpline(sketch, "E222.0.22", {"points": [v(-7.13, -2.82) * mm, v(-7.16, -3) * mm, v(-7.23, -3.33) * mm, v(-7.67, -3.64) * mm, v(-8.23, -3.67) * mm, v(-8.42, -3.67) * mm, v(-8.5, -3.66) * mm]});
            skLineSegment(sketch, "E222.0.23", {"start": v(-8.5, -3.66) * mm, "end": v(-8.85, -3.66) * mm});
            skLineSegment(sketch, "E222.0.24", {"start": v(-8.85, -3.66) * mm, "end": v(-8.85, -4.23) * mm});
            skLineSegment(sketch, "E222.0.25", {"start": v(-8.85, -4.23) * mm, "end": v(-2.68, -4.23) * mm});
            skLineSegment(sketch, "E222.0.26", {"start": v(-2.68, -4.23) * mm, "end": v(-2.68, -3.75) * mm});
            skLineSegment(sketch, "E222.0.27", {"start": v(-2.68, -3.75) * mm, "end": v(-3.08, -3.75) * mm});
            skFitSpline(sketch, "E222.0.28", {"points": [v(-3.08, -3.75) * mm, v(-3.33, -3.68) * mm, v(-3.77, -3.54) * mm, v(-4.14, -3.2) * mm, v(-4.24, -2.92) * mm, v(-4.28, -2.78) * mm]});
            skLineSegment(sketch, "E222.0.29", {"start": v(-4.28, -2.78) * mm, "end": v(-4.28, 1.1) * mm});
            skLineSegment(sketch, "E222.0.30", {"start": v(-4.28, 1.1) * mm, "end": v(0.7, 1.1) * mm});
            skLineSegment(sketch, "E222.0.31", {"start": v(0.7, 1.1) * mm, "end": v(0.7, -2.6) * mm});
            skFitSpline(sketch, "E222.0.32", {"points": [v(0.7, -2.6) * mm, v(0.71, -2.8) * mm, v(0.72, -3.2) * mm, v(0.34, -3.75) * mm, v(-0.24, -3.75) * mm, v(-0.53, -3.75) * mm, v(-0.67, -3.75) * mm]});
            skLineSegment(sketch, "E222.0.33", {"start": v(-0.67, -3.75) * mm, "end": v(-1, -3.75) * mm});
            skLineSegment(sketch, "E222.0.34", {"start": v(-1, -3.75) * mm, "end": v(-1, -4.23) * mm});
            skLineSegment(sketch, "E222.0.35", {"start": v(-1, -4.23) * mm, "end": v(5.21, -4.23) * mm});
            skLineSegment(sketch, "E223.0.0", {"start": v(16.2, 8.38) * mm, "end": v(15.06, 9.86) * mm});
            skLineSegment(sketch, "E223.0.1", {"start": v(15.06, 9.86) * mm, "end": v(11.34, 7.83) * mm});
            skLineSegment(sketch, "E223.0.2", {"start": v(11.34, 7.83) * mm, "end": v(11.73, 7.26) * mm});
            skLineSegment(sketch, "E223.0.3", {"start": v(11.73, 7.26) * mm, "end": v(16.2, 8.38) * mm});
            skLineSegment(sketch, "E224.0.0", {"start": v(-14.68, 4.01) * mm, "end": v(-14.68, -2.04) * mm});
            skFitSpline(sketch, "E224.0.1", {"points": [v(-14.68, -2.04) * mm, v(-14.7, -2.3) * mm, v(-14.7, -2.66) * mm, v(-14.64, -2.8) * mm, v(-15.16, -3.35) * mm, v(-15.73, -3.62) * mm, v(-15.94, -3.56) * mm, v(-15.86, -3.66) * mm, v(-15.96, -3.98) * mm, v(-15.75, -3.93) * mm, v(-15.4, -3.97) * mm, v(-14.9, -3.8) * mm, v(-13.68, -3.14) * mm, v(-13.2, -2.5) * mm, v(-12.96, -2) * mm, v(-12.84, -1.76) * mm]});
            skLineSegment(sketch, "E224.0.2", {"start": v(-12.84, -1.76) * mm, "end": v(-12.84, 4) * mm});
            skFitSpline(sketch, "E224.0.3", {"points": [v(-12.84, 4) * mm, v(-12.8, 4.12) * mm, v(-12.73, 4.38) * mm, v(-12.47, 4.39) * mm, v(-12.34, 4.4) * mm]});
            skLineSegment(sketch, "E224.0.4", {"start": v(-12.34, 4.4) * mm, "end": v(-11.81, 4.4) * mm});
            skLineSegment(sketch, "E224.0.5", {"start": v(-11.81, 4.4) * mm, "end": v(-11.81, 4.86) * mm});
            skLineSegment(sketch, "E224.0.6", {"start": v(-11.81, 4.86) * mm, "end": v(-15.63, 4.86) * mm});
            skLineSegment(sketch, "E224.0.7", {"start": v(-15.63, 4.86) * mm, "end": v(-15.63, 4.36) * mm});
            skLineSegment(sketch, "E224.0.8", {"start": v(-15.63, 4.36) * mm, "end": v(-15.1, 4.36) * mm});
            skFitSpline(sketch, "E224.0.9", {"points": [v(-15.1, 4.36) * mm, v(-14.97, 4.4) * mm, v(-14.71, 4.43) * mm, v(-14.7, 4.18) * mm, v(-14.68, 4.01) * mm]});
            skLineSegment(sketch, "E225.0.0", {"start": v(-18.55, 5.87) * mm, "end": v(-19.2, 6.79) * mm});
            skLineSegment(sketch, "E225.0.1", {"start": v(-19.2, 6.79) * mm, "end": v(-21.44, 5.5) * mm});
            skLineSegment(sketch, "E225.0.2", {"start": v(-21.44, 5.5) * mm, "end": v(-21.2, 5.16) * mm});
            skLineSegment(sketch, "E225.0.3", {"start": v(-21.2, 5.16) * mm, "end": v(-18.55, 5.87) * mm});
            skFitSpline(sketch, "E226.0.0", {"points": [v(-25.1, 4.44) * mm, v(-25, 4.37) * mm, v(-24.48, 4.56) * mm, v(-24.19, 4.26) * mm, v(-24.1, 3.92) * mm, v(-24.03, -0.08) * mm, v(-24.08, -0.34) * mm, v(-23.6, -1.8) * mm, v(-21.33, -2.46) * mm, v(-19.3, -2.45) * mm, v(-17.63, -0.88) * mm, v(-17.5, 0.29) * mm, v(-17.4, 3.43) * mm, v(-17.47, 3.9) * mm, v(-17.33, 4.26) * mm, v(-16.72, 4.46) * mm, v(-16.3, 4.28) * mm, v(-16.36, 4.87) * mm, v(-16.52, 4.84) * mm, v(-19.33, 4.89) * mm, v(-19.51, 4.89) * mm, v(-19.5, 4.8) * mm, v(-19.5, 4.48) * mm, v(-19.51, 4.34) * mm, v(-19.2, 4.47) * mm, v(-18.68, 4.43) * mm, v(-18.28, 4.3) * mm, v(-18.17, 3.73) * mm, v(-18.2, 3.58) * mm, v(-18.23, 0.08) * mm, v(-18.17, -0.11) * mm, v(-18.4, -0.7) * mm, v(-19.36, -1.62) * mm, v(-20.85, -1.74) * mm, v(-21.73, -1.2) * mm, v(-22.39, -0.29) * mm, v(-22.28, 0.5) * mm, v(-22.3, 0.62) * mm, v(-22.31, 3.95) * mm, v(-22.25, 4.05) * mm, v(-22.16, 4.4) * mm, v(-21.65, 4.46) * mm, v(-21.35, 4.36) * mm, v(-21.29, 4.61) * mm, v(-21.36, 4.73) * mm, v(-21.32, 4.93) * mm, v(-21.55, 4.83) * mm, v(-24.91, 4.76) * mm, v(-25.1, 4.9) * mm, v(-25.14, 4.71) * mm, v(-25.17, 4.49) * mm, v(-25.1, 4.44) * mm]});
            skFitSpline(sketch, "E227.0.0", {"points": [v(-18.55, -5.16) * mm, v(-18.79, -5.18) * mm, v(-19.52, -5.1) * mm, v(-21.1, -5.06) * mm, v(-21.97, -5.06) * mm, v(-22.58, -5.11) * mm, v(-23.17, -5.22) * mm, v(-23.95, -5.37) * mm, v(-24.9, -5.7) * mm, v(-25.93, -6.21) * mm, v(-26.53, -6.88) * mm, v(-26.9, -7.56) * mm, v(-27.07, -8.38) * mm, v(-26.87, -9.24) * mm, v(-26.6, -9.82) * mm, v(-26, -10.3) * mm, v(-25.25, -10.8) * mm, v(-23.91, -11.28) * mm, v(-22.47, -11.5) * mm, v(-20.87, -11.51) * mm, v(-19.96, -11.42) * mm, v(-19.08, -11.38) * mm, v(-18.61, -11.25) * mm, v(-18.56, -11.28) * mm, v(-18.47, -11.01) * mm, v(-18.1, -10.47) * mm, v(-17.79, -9.8) * mm, v(-17.7, -9.74) * mm, v(-17.82, -9.7) * mm, v(-18.36, -9.7) * mm, v(-18.4, -9.66) * mm, v(-18.47, -9.75) * mm, v(-18.57, -9.9) * mm, v(-18.93, -10.31) * mm, v(-19.68, -10.8) * mm, v(-20.35, -10.98) * mm, v(-21.58, -11.03) * mm, v(-23.04, -10.84) * mm, v(-23.8, -10.05) * mm, v(-24.39, -9.2) * mm, v(-24.57, -7.93) * mm, v(-24.22, -6.97) * mm, v(-23.9, -6.42) * mm, v(-23.04, -5.9) * mm, v(-22.32, -5.61) * mm, v(-21.28, -5.43) * mm, v(-20.47, -5.47) * mm, v(-20, -5.59) * mm, v(-19.33, -5.93) * mm, v(-19, -6.34) * mm, v(-18.67, -6.6) * mm, v(-18.63, -6.8) * mm, v(-18.62, -6.85) * mm, v(-18.53, -6.9) * mm, v(-18.08, -6.85) * mm, v(-18.03, -6.83) * mm, v(-18.1, -6.48) * mm, v(-18.1, -6.12) * mm, v(-18.13, -5.63) * mm, v(-18.15, -5.08) * mm, v(-18.4, -5.15) * mm, v(-18.55, -5.16) * mm]});
            skFitSpline(sketch, "E228.0.0", {"points": [v(-10.44, -9) * mm, v(-10.4, -8.91) * mm, v(-10.32, -8.72) * mm, v(-10.27, -8.24) * mm, v(-11.14, -7.15) * mm, v(-12.22, -7) * mm, v(-13.53, -6.9) * mm, v(-14.76, -7.18) * mm, v(-15.54, -7.62) * mm, v(-16.42, -8.23) * mm, v(-16.75, -9.19) * mm, v(-16.64, -10.1) * mm, v(-16.06, -10.8) * mm, v(-14.93, -11.31) * mm, v(-13.93, -11.47) * mm, v(-12.61, -11.46) * mm, v(-11.94, -11.27) * mm, v(-11.03, -10.88) * mm, v(-10.58, -10.62) * mm, v(-10.44, -10.44) * mm, v(-10.41, -10.32) * mm, v(-10.68, -10.23) * mm, v(-10.82, -10.2) * mm, v(-11.04, -10.34) * mm, v(-11.28, -10.46) * mm, v(-11.62, -10.57) * mm, v(-11.73, -10.59) * mm]});
            skFitSpline(sketch, "E228.0.1", {"points": [v(-11.73, -10.59) * mm, v(-11.84, -10.6) * mm, v(-12.1, -10.64) * mm, v(-12.76, -10.68) * mm, v(-13.42, -10.53) * mm, v(-14.13, -10.3) * mm, v(-14.48, -9.72) * mm, v(-14.66, -9.36) * mm, v(-14.7, -9.15) * mm, v(-14.7, -9.02) * mm, v(-14.7, -8.97) * mm, v(-14.65, -8.99) * mm, v(-14.61, -9) * mm]});
            skLineSegment(sketch, "E228.0.2", {"start": v(-14.61, -9) * mm, "end": v(-10.44, -9) * mm});
            skLineSegment(sketch, "E229.0.0", {"start": v(-1.1, -11.37) * mm, "end": v(-1.1, -10.98) * mm});
            skLineSegment(sketch, "E229.0.1", {"start": v(-1.1, -10.98) * mm, "end": v(-1.33, -10.98) * mm});
            skFitSpline(sketch, "E229.0.2", {"points": [v(-1.33, -10.98) * mm, v(-1.45, -11) * mm, v(-1.67, -11.02) * mm, v(-1.96, -10.85) * mm, v(-2.01, -10.74) * mm, v(-2.04, -10.69) * mm]});
            skLineSegment(sketch, "E229.0.3", {"start": v(-2.04, -10.69) * mm, "end": v(-2.04, -8.28) * mm});
            skFitSpline(sketch, "E229.0.4", {"points": [v(-2.04, -8.28) * mm, v(-2.05, -8.2) * mm, v(-2.06, -8.02) * mm, v(-2.17, -7.76) * mm, v(-2.38, -7.53) * mm, v(-2.68, -7.33) * mm, v(-2.99, -7.17) * mm, v(-3.22, -7.08) * mm, v(-3.44, -7.02) * mm, v(-3.7, -6.97) * mm, v(-3.97, -6.94) * mm, v(-4.22, -6.93) * mm, v(-4.42, -6.94) * mm, v(-4.64, -6.97) * mm, v(-4.87, -7) * mm, v(-5.08, -7.06) * mm, v(-5.26, -7.11) * mm, v(-5.44, -7.18) * mm, v(-5.62, -7.25) * mm, v(-5.78, -7.31) * mm, v(-5.89, -7.36) * mm, v(-5.99, -7.4) * mm, v(-6.12, -7.46) * mm, v(-6.3, -7.55) * mm, v(-6.43, -7.6) * mm, v(-6.5, -7.64) * mm, v(-6.52, -7.64) * mm, v(-6.5, -7.6) * mm, v(-6.5, -7.4) * mm, v(-6.5, -7.2) * mm, v(-6.5, -7.07) * mm, v(-6.5, -7.02) * mm, v(-6.5, -7) * mm, v(-6.5, -7) * mm, v(-6.52, -7) * mm, v(-6.58, -7) * mm, v(-6.68, -7) * mm, v(-6.85, -7.02) * mm, v(-7.07, -7.04) * mm, v(-7.36, -7.1) * mm, v(-7.65, -7.17) * mm, v(-7.98, -7.23) * mm, v(-8.26, -7.26) * mm, v(-8.56, -7.28) * mm, v(-8.85, -7.28) * mm, v(-9.1, -7.28) * mm, v(-9.25, -7.28) * mm, v(-9.32, -7.27) * mm, v(-9.34, -7.27) * mm, v(-9.35, -7.27) * mm, v(-9.35, -7.3) * mm, v(-9.35, -7.33) * mm, v(-9.36, -7.4) * mm, v(-9.38, -7.53) * mm, v(-9.37, -7.64) * mm, v(-9.28, -7.65) * mm, v(-9.16, -7.61) * mm, v(-9.06, -7.6) * mm, v(-8.97, -7.6) * mm, v(-8.86, -7.63) * mm, v(-8.73, -7.66) * mm, v(-8.64, -7.72) * mm, v(-8.6, -7.82) * mm, v(-8.58, -7.9) * mm, v(-8.57, -7.94) * mm]});
            skLineSegment(sketch, "E229.0.5", {"start": v(-8.57, -7.94) * mm, "end": v(-8.57, -10.62) * mm});
            skFitSpline(sketch, "E229.0.6", {"points": [v(-8.57, -10.62) * mm, v(-8.58, -10.7) * mm, v(-8.6, -10.88) * mm, v(-8.97, -11) * mm, v(-9.22, -11) * mm, v(-9.34, -11) * mm]});
            skLineSegment(sketch, "E229.0.7", {"start": v(-9.34, -11) * mm, "end": v(-9.63, -11) * mm});
            skLineSegment(sketch, "E229.0.8", {"start": v(-9.63, -11) * mm, "end": v(-9.63, -11.37) * mm});
            skLineSegment(sketch, "E229.0.9", {"start": v(-9.63, -11.37) * mm, "end": v(-5.63, -11.37) * mm});
            skLineSegment(sketch, "E229.0.10", {"start": v(-5.63, -11.37) * mm, "end": v(-5.63, -10.98) * mm});
            skLineSegment(sketch, "E229.0.11", {"start": v(-5.63, -10.98) * mm, "end": v(-5.8, -11) * mm});
            skFitSpline(sketch, "E229.0.12", {"points": [v(-5.8, -11) * mm, v(-5.9, -11.01) * mm, v(-6.14, -11.02) * mm, v(-6.32, -10.8) * mm, v(-6.5, -10.65) * mm, v(-6.5, -10.59) * mm]});
            skLineSegment(sketch, "E229.0.13", {"start": v(-6.5, -10.59) * mm, "end": v(-6.5, -7.96) * mm});
            skFitSpline(sketch, "E229.0.14", {"points": [v(-6.5, -7.96) * mm, v(-6.39, -7.92) * mm, v(-6.06, -7.86) * mm, v(-5.7, -7.65) * mm, v(-5.1, -7.61) * mm, v(-4.62, -7.69) * mm, v(-4.3, -8.05) * mm, v(-4.24, -8.22) * mm, v(-4.21, -8.3) * mm]});
            skLineSegment(sketch, "E229.0.15", {"start": v(-4.21, -8.3) * mm, "end": v(-4.21, -10.74) * mm});
            skFitSpline(sketch, "E229.0.16", {"points": [v(-4.21, -10.74) * mm, v(-4.23, -10.78) * mm, v(-4.27, -10.89) * mm, v(-4.45, -10.98) * mm, v(-4.6, -10.98) * mm, v(-4.69, -10.98) * mm]});
            skLineSegment(sketch, "E229.0.17", {"start": v(-4.69, -10.98) * mm, "end": v(-4.98, -10.98) * mm});
            skLineSegment(sketch, "E229.0.18", {"start": v(-4.98, -10.98) * mm, "end": v(-4.98, -11.37) * mm});
            skLineSegment(sketch, "E229.0.19", {"start": v(-4.98, -11.37) * mm, "end": v(-1.1, -11.37) * mm});
            skLineSegment(sketch, "E230.0.0", {"start": v(0.43, -7.53) * mm, "end": v(0.43, -10.53) * mm});
            skFitSpline(sketch, "E230.0.1", {"points": [v(0.43, -10.53) * mm, v(0.46, -10.62) * mm, v(0.53, -10.82) * mm, v(0.84, -11.15) * mm, v(1.32, -11.36) * mm, v(2.09, -11.5) * mm, v(2.79, -11.49) * mm, v(3.72, -11.26) * mm, v(4.3, -11.08) * mm, v(4.54, -11.01) * mm, v(4.49, -10.77) * mm, v(4.36, -10.68) * mm, v(4.13, -10.67) * mm, v(3.9, -10.8) * mm, v(3.47, -10.9) * mm, v(3.03, -10.75) * mm, v(2.68, -10.65) * mm, v(2.65, -10.45) * mm, v(2.64, -10.35) * mm]});
            skLineSegment(sketch, "E230.0.2", {"start": v(2.64, -10.35) * mm, "end": v(2.64, -7.53) * mm});
            skLineSegment(sketch, "E230.0.3", {"start": v(2.64, -7.53) * mm, "end": v(4.31, -7.53) * mm});
            skLineSegment(sketch, "E230.0.4", {"start": v(4.31, -7.53) * mm, "end": v(4.31, -7.02) * mm});
            skLineSegment(sketch, "E230.0.5", {"start": v(4.31, -7.02) * mm, "end": v(2.64, -7.02) * mm});
            skLineSegment(sketch, "E230.0.6", {"start": v(2.64, -7.02) * mm, "end": v(2.64, -5.7) * mm});
            skLineSegment(sketch, "E230.0.7", {"start": v(2.64, -5.7) * mm, "end": v(2.15, -5.7) * mm});
            skLineSegment(sketch, "E230.0.8", {"start": v(2.15, -5.7) * mm, "end": v(0.43, -6.4) * mm});
            skLineSegment(sketch, "E230.0.9", {"start": v(0.43, -6.4) * mm, "end": v(0.43, -7.02) * mm});
            skLineSegment(sketch, "E230.0.10", {"start": v(0.43, -7.02) * mm, "end": v(-0.2, -7.02) * mm});
            skLineSegment(sketch, "E230.0.11", {"start": v(-0.2, -7.02) * mm, "end": v(-0.73, -7.53) * mm});
            skLineSegment(sketch, "E230.0.12", {"start": v(-0.73, -7.53) * mm, "end": v(0.43, -7.53) * mm});
            skLineSegment(sketch, "E231.0.0", {"start": v(19.3, -10.56) * mm, "end": v(19.3, -7.08) * mm});
            skLineSegment(sketch, "E231.0.1", {"start": v(19.3, -7.08) * mm, "end": v(16.1, -7.17) * mm});
            skLineSegment(sketch, "E231.0.2", {"start": v(16.1, -7.17) * mm, "end": v(16.11, -7.5) * mm});
            skFitSpline(sketch, "E231.0.3", {"points": [v(16.11, -7.5) * mm, v(16.17, -7.5) * mm, v(16.3, -7.5) * mm, v(16.55, -7.49) * mm, v(16.85, -7.58) * mm, v(17, -7.7) * mm, v(17.07, -7.77) * mm]});
            skLineSegment(sketch, "E231.0.4", {"start": v(17.07, -7.77) * mm, "end": v(17.07, -10.43) * mm});
            skFitSpline(sketch, "E231.0.5", {"points": [v(17.07, -10.43) * mm, v(16.98, -10.5) * mm, v(16.8, -10.62) * mm, v(16.51, -10.7) * mm, v(16.11, -10.76) * mm, v(15.7, -10.74) * mm, v(15.4, -10.7) * mm, v(15.03, -10.42) * mm, v(14.92, -10.18) * mm, v(14.88, -10) * mm, v(14.85, -9.91) * mm]});
            skLineSegment(sketch, "E231.0.6", {"start": v(14.85, -9.91) * mm, "end": v(14.85, -7.04) * mm});
            skLineSegment(sketch, "E231.0.7", {"start": v(14.85, -7.04) * mm, "end": v(11.89, -7.14) * mm});
            skLineSegment(sketch, "E231.0.8", {"start": v(11.89, -7.14) * mm, "end": v(11.9, -7.54) * mm});
            skFitSpline(sketch, "E231.0.9", {"points": [v(11.9, -7.54) * mm, v(11.97, -7.53) * mm, v(12.1, -7.52) * mm, v(12.4, -7.59) * mm, v(12.66, -7.66) * mm, v(12.73, -7.8) * mm, v(12.77, -7.86) * mm]});
            skLineSegment(sketch, "E231.0.10", {"start": v(12.77, -7.86) * mm, "end": v(12.77, -10.35) * mm});
            skFitSpline(sketch, "E231.0.11", {"points": [v(12.77, -10.35) * mm, v(12.76, -10.4) * mm, v(12.75, -10.5) * mm, v(12.83, -10.67) * mm, v(12.97, -10.9) * mm, v(13.38, -11.16) * mm, v(13.88, -11.42) * mm, v(14.52, -11.48) * mm, v(15.33, -11.52) * mm, v(15.84, -11.37) * mm, v(16.43, -11.17) * mm, v(16.74, -10.98) * mm, v(16.95, -10.91) * mm, v(17.06, -10.88) * mm]});
            skLineSegment(sketch, "E231.0.12", {"start": v(17.06, -10.88) * mm, "end": v(17.06, -11.45) * mm});
            skFitSpline(sketch, "E231.0.13", {"points": [v(17.06, -11.45) * mm, v(17.2, -11.4) * mm, v(17.72, -11.32) * mm, v(18.21, -11.26) * mm, v(18.8, -11.18) * mm, v(19.54, -11.08) * mm, v(20.23, -11.1) * mm, v(20.28, -11.1) * mm, v(20.27, -10.9) * mm, v(20.28, -10.65) * mm, v(19.9, -10.77) * mm, v(19.41, -10.66) * mm, v(19.3, -10.56) * mm]});
            skFitSpline(sketch, "E232.0.0", {"points": [v(30.73, -10.82) * mm, v(30.7, -10.9) * mm, v(30.6, -10.96) * mm, v(30.39, -11.02) * mm, v(30.28, -11.01) * mm, v(30.22, -11) * mm]});
            skLineSegment(sketch, "E232.0.1", {"start": v(30.22, -11) * mm, "end": v(29.94, -11) * mm});
            skLineSegment(sketch, "E232.0.2", {"start": v(29.94, -11) * mm, "end": v(29.94, -11.4) * mm});
            skLineSegment(sketch, "E232.0.3", {"start": v(29.94, -11.4) * mm, "end": v(33.83, -11.4) * mm});
            skLineSegment(sketch, "E232.0.4", {"start": v(33.83, -11.4) * mm, "end": v(33.83, -10.97) * mm});
            skLineSegment(sketch, "E232.0.5", {"start": v(33.83, -10.97) * mm, "end": v(33.61, -10.98) * mm});
            skFitSpline(sketch, "E232.0.6", {"points": [v(33.61, -10.98) * mm, v(33.55, -10.98) * mm, v(33.42, -11) * mm, v(33.08, -10.88) * mm, v(32.99, -10.79) * mm, v(32.95, -10.75) * mm]});
            skLineSegment(sketch, "E232.0.7", {"start": v(32.95, -10.75) * mm, "end": v(32.95, -8.3) * mm});
            skFitSpline(sketch, "E232.0.8", {"points": [v(32.95, -8.3) * mm, v(32.92, -8.16) * mm, v(32.87, -7.9) * mm, v(32.68, -7.57) * mm, v(32.23, -7.23) * mm, v(31.7, -7.1) * mm, v(31.1, -6.95) * mm, v(30.3, -6.96) * mm, v(29.7, -7.14) * mm, v(29.1, -7.38) * mm, v(28.7, -7.6) * mm, v(28.42, -7.77) * mm, v(28.35, -7.8) * mm, v(28.32, -7.67) * mm, v(27.99, -7.28) * mm, v(27.45, -7.02) * mm, v(26.8, -6.93) * mm, v(25.9, -6.97) * mm, v(25.42, -7.1) * mm, v(24.68, -7.37) * mm, v(24.43, -7.52) * mm, v(24.24, -7.59) * mm, v(24.15, -7.62) * mm]});
            skLineSegment(sketch, "E232.0.9", {"start": v(24.15, -7.62) * mm, "end": v(24.15, -6.96) * mm});
            skFitSpline(sketch, "E232.0.10", {"points": [v(24.15, -6.96) * mm, v(24.1, -6.99) * mm, v(23.9, -7.07) * mm, v(22.77, -7.22) * mm, v(22.1, -7.23) * mm, v(21.75, -7.23) * mm]});
            skLineSegment(sketch, "E232.0.11", {"start": v(21.75, -7.23) * mm, "end": v(21.11, -7.23) * mm});
            skLineSegment(sketch, "E232.0.12", {"start": v(21.11, -7.23) * mm, "end": v(21.12, -7.6) * mm});
            skLineSegment(sketch, "E232.0.13", {"start": v(21.12, -7.6) * mm, "end": v(21.56, -7.6) * mm});
            skFitSpline(sketch, "E232.0.14", {"points": [v(21.56, -7.6) * mm, v(21.6, -7.61) * mm, v(21.68, -7.65) * mm, v(21.87, -7.76) * mm, v(21.91, -7.85) * mm, v(21.94, -7.89) * mm]});
            skLineSegment(sketch, "E232.0.15", {"start": v(21.94, -7.89) * mm, "end": v(21.94, -10.72) * mm});
            skFitSpline(sketch, "E232.0.16", {"points": [v(21.94, -10.72) * mm, v(21.92, -10.76) * mm, v(21.87, -10.82) * mm, v(21.69, -10.96) * mm, v(21.26, -11.03) * mm, v(21.13, -11.02) * mm, v(21.07, -11.02) * mm]});
            skLineSegment(sketch, "E232.0.17", {"start": v(21.07, -11.02) * mm, "end": v(20.93, -11.02) * mm});
            skLineSegment(sketch, "E232.0.18", {"start": v(20.93, -11.02) * mm, "end": v(20.93, -11.4) * mm});
            skLineSegment(sketch, "E232.0.19", {"start": v(20.93, -11.4) * mm, "end": v(24.9, -11.4) * mm});
            skLineSegment(sketch, "E232.0.20", {"start": v(24.9, -11.4) * mm, "end": v(24.88, -11) * mm});
            skLineSegment(sketch, "E232.0.21", {"start": v(24.88, -11) * mm, "end": v(24.61, -11.02) * mm});
            skFitSpline(sketch, "E232.0.22", {"points": [v(24.61, -11.02) * mm, v(24.58, -11.02) * mm, v(24.5, -11) * mm, v(24.28, -10.98) * mm, v(24.16, -10.87) * mm, v(24.13, -10.79) * mm, v(24.11, -10.75) * mm]});
            skLineSegment(sketch, "E232.0.23", {"start": v(24.11, -10.75) * mm, "end": v(24.11, -8.08) * mm});
            skFitSpline(sketch, "E232.0.24", {"points": [v(24.11, -8.08) * mm, v(24.13, -8.04) * mm, v(24.18, -7.95) * mm, v(24.37, -7.84) * mm, v(24.91, -7.68) * mm, v(25.25, -7.68) * mm, v(25.88, -7.8) * mm, v(26.05, -7.95) * mm, v(26.25, -8.12) * mm, v(26.29, -8.25) * mm, v(26.3, -8.31) * mm]});
            skLineSegment(sketch, "E232.0.25", {"start": v(26.3, -8.31) * mm, "end": v(26.3, -10.76) * mm});
            skFitSpline(sketch, "E232.0.26", {"points": [v(26.3, -10.76) * mm, v(26.29, -10.8) * mm, v(26.24, -10.87) * mm, v(26.05, -10.96) * mm, v(25.88, -11.02) * mm, v(25.78, -11) * mm, v(25.73, -11) * mm]});
            skLineSegment(sketch, "E232.0.27", {"start": v(25.73, -11) * mm, "end": v(25.55, -11) * mm});
            skLineSegment(sketch, "E232.0.28", {"start": v(25.55, -11) * mm, "end": v(25.55, -11.4) * mm});
            skLineSegment(sketch, "E232.0.29", {"start": v(25.55, -11.4) * mm, "end": v(29.38, -11.4) * mm});
            skLineSegment(sketch, "E232.0.30", {"start": v(29.38, -11.4) * mm, "end": v(29.36, -11) * mm});
            skLineSegment(sketch, "E232.0.31", {"start": v(29.36, -11) * mm, "end": v(29.06, -11.02) * mm});
            skFitSpline(sketch, "E232.0.32", {"points": [v(29.06, -11.02) * mm, v(28.98, -11) * mm, v(28.84, -10.98) * mm, v(28.67, -10.9) * mm, v(28.6, -10.79) * mm, v(28.55, -10.73) * mm]});
            skLineSegment(sketch, "E232.0.33", {"start": v(28.55, -10.73) * mm, "end": v(28.55, -8.04) * mm});
            skFitSpline(sketch, "E232.0.34", {"points": [v(28.55, -8.04) * mm, v(28.6, -8.01) * mm, v(28.7, -7.93) * mm, v(29.25, -7.74) * mm, v(29.58, -7.73) * mm, v(29.96, -7.7) * mm, v(30.44, -7.83) * mm, v(30.72, -8.13) * mm, v(30.7, -8.3) * mm, v(30.73, -8.35) * mm]});
            skLineSegment(sketch, "E232.0.35", {"start": v(30.73, -8.35) * mm, "end": v(30.73, -10.82) * mm});
            skFitSpline(sketch, "E233.0.0", {"points": [v(8.26, -8.42) * mm, v(8.34, -8.38) * mm, v(8.52, -8.27) * mm, v(8.86, -8.07) * mm, v(9.04, -7.98) * mm, v(9.38, -8.01) * mm, v(9.58, -8.11) * mm, v(9.8, -8.28) * mm, v(10.04, -8.39) * mm, v(10.55, -8.3) * mm, v(10.8, -8.18) * mm, v(11.07, -7.95) * mm, v(11.15, -7.65) * mm, v(11.18, -7.45) * mm, v(11.02, -7.23) * mm, v(10.76, -7.05) * mm, v(10.4, -6.93) * mm, v(9.84, -6.93) * mm, v(9.4, -7.03) * mm, v(9.11, -7.22) * mm, v(8.75, -7.43) * mm, v(8.42, -7.77) * mm, v(8.3, -7.88) * mm, v(8.26, -7.93) * mm]});
            skLineSegment(sketch, "E233.0.1", {"start": v(8.26, -7.93) * mm, "end": v(8.26, -6.9) * mm});
            skFitSpline(sketch, "E233.0.2", {"points": [v(8.26, -6.9) * mm, v(8.08, -6.94) * mm, v(7.85, -6.97) * mm, v(7.25, -7.13) * mm, v(6.73, -7.23) * mm, v(6.31, -7.3) * mm, v(6.19, -7.3) * mm, v(6.13, -7.3) * mm]});
            skLineSegment(sketch, "E233.0.3", {"start": v(6.13, -7.3) * mm, "end": v(5.24, -7.3) * mm});
            skLineSegment(sketch, "E233.0.4", {"start": v(5.24, -7.3) * mm, "end": v(5.24, -7.62) * mm});
            skLineSegment(sketch, "E233.0.5", {"start": v(5.24, -7.62) * mm, "end": v(5.53, -7.62) * mm});
            skFitSpline(sketch, "E233.0.6", {"points": [v(5.53, -7.62) * mm, v(5.57, -7.63) * mm, v(5.67, -7.65) * mm, v(5.95, -7.71) * mm, v(6.09, -7.86) * mm, v(6.12, -8) * mm, v(6.13, -8.07) * mm]});
            skLineSegment(sketch, "E233.0.7", {"start": v(6.13, -8.07) * mm, "end": v(6.13, -10.53) * mm});
            skFitSpline(sketch, "E233.0.8", {"points": [v(6.13, -10.53) * mm, v(6.11, -10.58) * mm, v(6.08, -10.68) * mm, v(5.98, -10.84) * mm, v(5.75, -10.98) * mm, v(5.5, -11.02) * mm, v(5.4, -11.01) * mm, v(5.37, -11) * mm]});
            skLineSegment(sketch, "E233.0.9", {"start": v(5.37, -11) * mm, "end": v(5.06, -11) * mm});
            skLineSegment(sketch, "E233.0.10", {"start": v(5.06, -11) * mm, "end": v(5.06, -11.36) * mm});
            skLineSegment(sketch, "E233.0.11", {"start": v(5.06, -11.36) * mm, "end": v(9.5, -11.36) * mm});
            skLineSegment(sketch, "E233.0.12", {"start": v(9.5, -11.36) * mm, "end": v(9.5, -10.98) * mm});
            skLineSegment(sketch, "E233.0.13", {"start": v(9.5, -10.98) * mm, "end": v(8.93, -10.98) * mm});
            skFitSpline(sketch, "E233.0.14", {"points": [v(8.93, -10.98) * mm, v(8.86, -10.98) * mm, v(8.71, -10.97) * mm, v(8.46, -10.9) * mm, v(8.3, -10.8) * mm, v(8.28, -10.67) * mm, v(8.26, -10.6) * mm]});
            skLineSegment(sketch, "E233.0.15", {"start": v(8.26, -10.6) * mm, "end": v(8.26, -8.42) * mm});
            skFitSpline(sketch, "E234.0.0", {"points": [v(-12.39, -8.57) * mm, v(-12.36, -8.58) * mm, v(-12.3, -8.6) * mm, v(-12.34, -8.38) * mm, v(-12.32, -8.18) * mm, v(-12.45, -7.84) * mm, v(-12.6, -7.6) * mm, v(-12.75, -7.47) * mm, v(-12.96, -7.34) * mm, v(-13.63, -7.36) * mm, v(-13.96, -7.52) * mm, v(-14.3, -7.8) * mm, v(-14.53, -8.14) * mm, v(-14.57, -8.42) * mm, v(-14.57, -8.53) * mm, v(-14.56, -8.57) * mm]});
            skLineSegment(sketch, "E234.0.1", {"start": v(-14.56, -8.57) * mm, "end": v(-12.39, -8.57) * mm});
            skSolve(sketch);
        }
        {
            var Q0;
            Q0=makeQuery(id+"F2.imprint","IMPRINT",FACE,{"disambiguationData":[TD([[makeQuery(id+"F2.imprint","IMPRINT",EDGE,{"derivedFrom":sQuery(id+"F2.wireOp",EDGE,"E217.0.0")}),1.0]])]});
            var Q1;
            Q1=makeQuery(id+"F2.imprint","IMPRINT",FACE,{"disambiguationData":[TD([[makeQuery(id+"F2.imprint","IMPRINT",EDGE,{"derivedFrom":sQuery(id+"F2.wireOp",EDGE,"E216.0.0")}),1.0]])]});
            var Q2;
            Q2=makeQuery(id+"F2.imprint","IMPRINT",FACE,{"disambiguationData":[TD([[makeQuery(id+"F2.imprint","IMPRINT",EDGE,{"derivedFrom":sQuery(id+"F2.wireOp",EDGE,"E226.0.0")}),1.0]])]});
            var Q3;
            Q3=makeQuery(id+"F2.imprint","IMPRINT",FACE,{"disambiguationData":[TD([[makeQuery(id+"F2.imprint","IMPRINT",EDGE,{"derivedFrom":sQuery(id+"F2.wireOp",EDGE,"E225.0.0")}),1.0]])]});
            var Q4;
            Q4=makeQuery(id+"F2.imprint","IMPRINT",FACE,{"disambiguationData":[TD([[makeQuery(id+"F2.imprint","IMPRINT",EDGE,{"derivedFrom":sQuery(id+"F2.wireOp",EDGE,"E224.0.0")}),1.0]])]});
            extrude(context, id + "F3", {"entities" : qUnion([Q0, Q1, Q2, Q3, Q4]), "operationType" : NewBodyOperationType.ADD, "depth" : 0.8 * mm, "offsetDistance" : 25 * mm});
        }
        {
            var Q0;
            Q0=makeQuery(id+"F1.opExtrude","CAP_FACE",FACE,{"disambiguationData":[OSD([sQuery(id+"F0.wireOp",EDGE,"E207"),sQuery(id+"F0.wireOp",EDGE,"E208"),sQuery(id+"F0.wireOp",EDGE,"E209"),sQuery(id+"F0.wireOp",EDGE,"E210"),sQuery(id+"F0.wireOp",EDGE,"E211"),sQuery(id+"F0.wireOp",EDGE,"E212"),sQuery(id+"F0.wireOp",EDGE,"E213"),sQuery(id+"F0.wireOp",EDGE,"E214"),sQuery(id+"F0.wireOp",EDGE,"E215")])],"isStart":true});
            var sketch = newSketch(context, id + "F4", { "sketchPlane" : qUnion([Q0])});
            skLineSegment(sketch, "E235", {"start": v(-30.8, -13.04) * mm, "end": v(35.92, 19.17) * mm, "construction": true});
            skLineSegment(sketch, "E236", {"start": v(34.68, -12.85) * mm, "end": v(-34.05, 15.76) * mm, "construction": true});
            skLineSegment(sketch, "E237", {"start": v(1.83, -25.26) * mm, "end": v(-2.14, 23.8) * mm, "construction": true});
            skLineSegment(sketch, "E238", {"start": v(8.36, 4.35) * mm, "end": v(-4.64, 4.35) * mm});
            skLineSegment(sketch, "E239", {"start": v(-4.64, 4.35) * mm, "end": v(1.86, -4.52) * mm});
            skLineSegment(sketch, "E240", {"start": v(1.86, -4.52) * mm, "end": v(8.36, 4.35) * mm});
            skSolve(sketch);
        }
        {
            var Q0;
            Q0=makeQuery(id+"F4.imprint","IMPRINT",FACE,{"disambiguationData":[TD([[makeQuery(id+"F4.imprint","IMPRINT",EDGE,{"derivedFrom":sQuery(id+"F4.wireOp",EDGE,"E238")}),1.0]])]});
            extrude(context, id + "F5", {"entities" : qUnion([Q0]), "operationType" : NewBodyOperationType.REMOVE, "oppositeDirection" : true, "depth" : 0.8 * mm, "offsetDistance" : 25 * mm});
        }
    });
